FCSTD DOCUMENT  (FreeCAD 0.19R23578 (Git))
Label: carriage_assembly
License: All rights reserved
LicenseURL: http://en.wikipedia.org/wiki/All_rights_reserved
objects: App::Link×16, App::DocumentObjectGroup×2, PartDesign::CoordinateSystem×2, App::FeaturePython×1, App::Part×1
note: 2 computed .brp shape members not serialized (recipe doc carries the construction recipe); baked Part::Feature solids carry a one-line shape summary decoded from their .brp
EXTERNAL_REF file=y_axis_carriage_block.FCStd obj=Part026
EXTERNAL_REF file=x_axis_rail.FCStd obj=LCS_2
EXTERNAL_REF file=y_axis_carriage_block.FCStd obj=LCS_4
EXTERNAL_REF file=x_axis_rail.FCStd obj=Part028
EXTERNAL_REF file=x_axis_rail.FCStd obj=LCS_1
EXTERNAL_REF file=x_idler_bracket.FCStd obj=LCS_1
EXTERNAL_REF file=x_idler_bracket.FCStd obj=Part033
EXTERNAL_REF file=gates_2gt_idler_toothed.FCStd obj=LCS_1
EXTERNAL_REF file=x_idler_bracket.FCStd obj=LCS_2
EXTERNAL_REF file=gates_2gt_idler_toothed.FCStd obj=Part042
EXTERNAL_REF file=stock_motor_mount.FCStd obj=LCS_6
EXTERNAL_REF file=y_axis_carriage_block.FCStd obj=LCS_15
EXTERNAL_REF file=stock_motor_mount.FCStd obj=Part
EXTERNAL_REF file=Nema 17  Stepper Motor length 60mm.FcStd obj=LCS_0
EXTERNAL_REF file=stock_motor_mount.FCStd obj=LCS_1
EXTERNAL_REF file=Nema 17  Stepper Motor length 60mm.FcStd obj=Part
EXTERNAL_REF file=Nema 17  Stepper Motor length 60mm.FcStd obj=LCS_1
EXTERNAL_REF file=2gt_pulley_20t.FCStd obj=LCS_1
EXTERNAL_REF file=2gt_pulley_20t.FCStd obj=Part
EXTERNAL_REF file=watercooled_print_head.FCStd obj=LCS_1
EXTERNAL_REF file=x_axis_rail.FCStd obj=LCS_3
EXTERNAL_REF file=watercooled_print_head.FCStd obj=Model
EXTERNAL_REF file=Aluminum Spacer 6mm002.FCStd obj=LCS_1
EXTERNAL_REF file=y_axis_carriage_block.FCStd obj=LCS_12
EXTERNAL_REF file=Aluminum Spacer 6mm002.FCStd obj=Aluminum_Spacer_6mm002
EXTERNAL_REF file=y_axis_carriage_block.FCStd obj=LCS_11
EXTERNAL_REF file=eccentric_spacer.FCStd obj=LCS_1
EXTERNAL_REF file=y_axis_carriage_block.FCStd obj=LCS_13
EXTERNAL_REF file=eccentric_spacer.FCStd obj=Part
EXTERNAL_REF file=y_axis_carriage_block.FCStd obj=LCS_14
EXTERNAL_REF file=Aluminum Spacer 6mm002.FCStd obj=LCS_2
EXTERNAL_REF file=solid_v_wheel_assembly.FCStd obj=LCS_Origin
EXTERNAL_REF file=solid_v_wheel_assembly.FCStd obj=Model
EXTERNAL_REF file=eccentric_spacer.FCStd obj=LCS_2

FEATURE [App::DocumentObjectGroup] Parts
FEATURE [PartDesign::CoordinateSystem] LCS_Origin
  AttacherType = Attacher::AttachEngine3D
  MapMode = 2
  Support = -> [X_Axis]
FEATURE [App::DocumentObjectGroup] Constraints
FEATURE [App::FeaturePython] Variables  # WARN: FeaturePython — macro-defined, semantics opaque (R4)
FEATURE [App::Link] y_axis_carriage_block_y_axis_carriage_block001
  LinkedObject = -> <external y_axis_carriage_block.FCStd>#Part026
FEATURE [App::Link] x_axis_rail_2020_vslot_rail
  AssemblyType = Asm4EE
  AttachedBy = #LCS_2
  AttachedTo = y_axis_carriage_block_y_axis_carriage_block001#LCS_4
  AttachmentOffset = pos=(0,0,0) rot=(0,1,0;4.71239rad)
  LinkPlacement = pos=(57.675,-10,-1.34e-14) rot=(0.57735,-0.57735,0.57735;4.18879rad)
  LinkedObject = -> <external x_axis_rail.FCStd>#Part028
  Placement = pos=(57.675,-10,-1.34e-14) rot=(0.57735,-0.57735,0.57735;4.18879rad)
  expr: Placement = y_axis_carriage_block_y_axis_carriage_block001.Placement * y_axis_carriage_block#LCS_4.Placement * AttachmentOffset * x_axis_rail#LCS_2.Placement ^ -1
FEATURE [App::Link] x_idler_bracket_x_idler_bracket
  AssemblyType = Asm4EE
  AttachedBy = #LCS_1
  AttachedTo = x_axis_rail_2020_vslot_rail#LCS_1
  AttachmentOffset = pos=(0,0,0) rot=(0,0,1;4.71239rad)
  LinkPlacement = pos=(437.675,-10,-2.064e-13) rot=(0,0,1;0rad)
  LinkedObject = -> <external x_idler_bracket.FCStd>#Part033
  Placement = pos=(437.675,-10,-2.064e-13) rot=(0,0,1;0rad)
  expr: Placement = x_axis_rail_2020_vslot_rail.Placement * x_axis_rail#LCS_1.Placement * AttachmentOffset * x_idler_bracket#LCS_1.Placement ^ -1
FEATURE [App::Link] gates_2gt_idler_toothed_e3d_2gt_idler
  AssemblyType = Asm4EE
  AttachedBy = #LCS_1
  AttachedTo = x_idler_bracket_x_idler_bracket#LCS_2
  LinkPlacement = pos=(448.675,-24,-2.846e-13) rot=(-0.57735,-0.57735,-0.57735;2.0944rad)
  LinkedObject = -> <external gates_2gt_idler_toothed.FCStd>#Part042
  Placement = pos=(448.675,-24,-2.846e-13) rot=(-0.57735,-0.57735,-0.57735;2.0944rad)
  expr: Placement = x_idler_bracket_x_idler_bracket.Placement * x_idler_bracket#LCS_2.Placement * AttachmentOffset * gates_2gt_idler_toothed#LCS_1.Placement ^ -1
FEATURE [App::Link] stock_motor_mount_stock_motor_mount
  AssemblyType = Asm4EE
  AttachedBy = #LCS_6
  AttachedTo = y_axis_carriage_block_y_axis_carriage_block001#LCS_15
  LinkPlacement = pos=(9.35,-23,-36) rot=(0.57735,0.57735,0.57735;4.18879rad)
  LinkedObject = -> <external stock_motor_mount.FCStd>#Part
  Placement = pos=(9.35,-23,-36) rot=(0.57735,0.57735,0.57735;4.18879rad)
  expr: Placement = y_axis_carriage_block_y_axis_carriage_block001.Placement * y_axis_carriage_block#LCS_15.Placement * AttachmentOffset * stock_motor_mount#LCS_6.Placement ^ -1
FEATURE [App::Link] Nema_17__Stepper_Motor_length_60mm_Nema_17__Stepper_Motor_length_60mm  label="Nema_17__Stepper_Motor_length_60mm_Nema 17  Stepper Motor length 60mm"
  AssemblyType = Asm4EE
  AttachedBy = #LCS_0
  AttachedTo = stock_motor_mount_stock_motor_mount#LCS_1
  AttachmentOffset = pos=(0,0,0) rot=(1,0,0;3.14159rad)
  LinkPlacement = pos=(36.33,-23,73.42) rot=(0,0.707107,0.707107;3.14159rad)
  LinkedObject = -> <external Nema 17  Stepper Motor length 60mm.FcStd>#Part
  Placement = pos=(36.33,-23,73.42) rot=(0,0.707107,0.707107;3.14159rad)
  expr: Placement = stock_motor_mount_stock_motor_mount.Placement * stock_motor_mount#LCS_1.Placement * AttachmentOffset * Nema_17__Stepper_Motor_length_60mm#LCS_0.Placement ^ -1
FEATURE [App::Link] _gt_pulley_20t_2gt_pulley_20t
  AssemblyType = Asm4EE
  AttachedBy = #LCS_1
  AttachedTo = Nema_17__Stepper_Motor_length_60mm_Nema_17__Stepper_Motor_length_60mm#LCS_1
  AttachmentOffset = pos=(0,0,0) rot=(1,0,0;3.14159rad)
  LinkPlacement = pos=(36.33,-23,-10.18) rot=(-0.57735,-0.57735,-0.57735;2.0944rad)
  LinkedObject = -> <external 2gt_pulley_20t.FCStd>#Part
  Placement = pos=(36.33,-23,-10.18) rot=(-0.57735,-0.57735,-0.57735;2.0944rad)
  expr: Placement = Nema_17__Stepper_Motor_length_60mm_Nema_17__Stepper_Motor_length_60mm.Placement * Nema_17__Stepper_Motor_length_60mm#LCS_1.Placement * AttachmentOffset * _gt_pulley_20t#LCS_1.Placement ^ -1
FEATURE [App::Link] watercooled_print_head
  AssemblyType = Asm4EE
  AttachedBy = #LCS_1
  AttachedTo = x_axis_rail_2020_vslot_rail#LCS_3
  AttachmentOffset = pos=(0,0,0) rot=(0.57735,-0.57735,0.57735;2.0944rad)
  LinkPlacement = pos=(241.675,-40,-25) rot=(0,0,1;0rad)
  LinkedObject = -> <external watercooled_print_head.FCStd>#Model
  Placement = pos=(241.675,-40,-25) rot=(0,0,1;0rad)
  expr: Placement = x_axis_rail_2020_vslot_rail.Placement * x_axis_rail#LCS_3.Placement * AttachmentOffset * watercooled_print_head#LCS_1.Placement ^ -1
FEATURE [App::Link] Aluminum_Spacer_6mm002_Aluminum_Spacer_6mm002
  AssemblyType = Asm4EE
  AttachedBy = #LCS_1
  AttachedTo = y_axis_carriage_block_y_axis_carriage_block001#LCS_12
  LinkPlacement = pos=(-6,40,49.85) rot=(0,-1,0;4.71239rad)
  LinkedObject = -> <external Aluminum Spacer 6mm002.FCStd>#Aluminum_Spacer_6mm002
  Placement = pos=(-6,40,49.85) rot=(0,-1,0;4.71239rad)
  expr: Placement = y_axis_carriage_block_y_axis_carriage_block001.Placement * y_axis_carriage_block#LCS_12.Placement * AttachmentOffset * Aluminum_Spacer_6mm002#LCS_1.Placement ^ -1
FEATURE [App::Link] Aluminum_Spacer_6mm002_Aluminum_Spacer_6mm003
  AssemblyType = Asm4EE
  AttachedBy = #LCS_1
  AttachedTo = y_axis_carriage_block_y_axis_carriage_block001#LCS_11
  LinkPlacement = pos=(-6,-40,49.85) rot=(0,-1,0;4.71239rad)
  LinkedObject = -> <external Aluminum Spacer 6mm002.FCStd>#Aluminum_Spacer_6mm002
  Placement = pos=(-6,-40,49.85) rot=(0,-1,0;4.71239rad)
  expr: Placement = y_axis_carriage_block_y_axis_carriage_block001.Placement * y_axis_carriage_block#LCS_11.Placement * AttachmentOffset * Aluminum_Spacer_6mm002#LCS_1.Placement ^ -1
FEATURE [App::Link] eccentric_spacer_eccentric_spacer
  AssemblyType = Asm4EE
  AttachedBy = #LCS_1
  AttachedTo = y_axis_carriage_block_y_axis_carriage_block001#LCS_13
  AttachmentOffset = pos=(0,0,0) rot=(1,0,0;3.14159rad)
  LinkPlacement = pos=(0,40,-49.85) rot=(-0.707107,0,0.707107;3.14159rad)
  LinkedObject = -> <external eccentric_spacer.FCStd>#Part
  Placement = pos=(0,40,-49.85) rot=(-0.707107,0,0.707107;3.14159rad)
  expr: Placement = y_axis_carriage_block_y_axis_carriage_block001.Placement * y_axis_carriage_block#LCS_13.Placement * AttachmentOffset * eccentric_spacer#LCS_1.Placement ^ -1
FEATURE [App::Link] eccentric_spacer_eccentric_spacer_2
  AssemblyType = Asm4EE
  AttachedBy = #LCS_1
  AttachedTo = y_axis_carriage_block_y_axis_carriage_block001#LCS_14
  AttachmentOffset = pos=(0,0,0) rot=(0,-1,0;3.14159rad)
  LinkPlacement = pos=(0,-40,-49.85) rot=(0,-1,0;1.5708rad)
  LinkedObject = -> <external eccentric_spacer.FCStd>#Part
  Placement = pos=(0,-40,-49.85) rot=(0,-1,0;1.5708rad)
  expr: Placement = y_axis_carriage_block_y_axis_carriage_block001.Placement * y_axis_carriage_block#LCS_14.Placement * AttachmentOffset * eccentric_spacer#LCS_1.Placement ^ -1
FEATURE [App::Link] solid_v_wheel_assembly
  AssemblyType = Asm4EE
  AttachedBy = #LCS_Origin
  AttachedTo = Aluminum_Spacer_6mm002_Aluminum_Spacer_6mm002#LCS_2
  LinkPlacement = pos=(-6,40,49.85) rot=(0.57735,-0.57735,0.57735;4.18879rad)
  LinkedObject = -> <external solid_v_wheel_assembly.FCStd>#Model
  Placement = pos=(-6,40,49.85) rot=(0.57735,-0.57735,0.57735;4.18879rad)
  expr: Placement = Aluminum_Spacer_6mm002_Aluminum_Spacer_6mm002.Placement * Aluminum_Spacer_6mm002#LCS_2.Placement * AttachmentOffset * solid_v_wheel_assembly#LCS_Origin.Placement ^ -1
FEATURE [App::Link] solid_v_wheel_assembly_2
  AssemblyType = Asm4EE
  AttachedBy = #LCS_Origin
  AttachedTo = Aluminum_Spacer_6mm002_Aluminum_Spacer_6mm003#LCS_2
  LinkPlacement = pos=(-6,-40,49.85) rot=(0.57735,-0.57735,0.57735;4.18879rad)
  LinkedObject = -> <external solid_v_wheel_assembly.FCStd>#Model
  Placement = pos=(-6,-40,49.85) rot=(0.57735,-0.57735,0.57735;4.18879rad)
  expr: Placement = Aluminum_Spacer_6mm002_Aluminum_Spacer_6mm003.Placement * Aluminum_Spacer_6mm002#LCS_2.Placement * AttachmentOffset * solid_v_wheel_assembly#LCS_Origin.Placement ^ -1
FEATURE [App::Link] solid_v_wheel_assembly_3
  AssemblyType = Asm4EE
  AttachedBy = #LCS_Origin
  AttachedTo = eccentric_spacer_eccentric_spacer#LCS_2
  AttachmentOffset = pos=(0,0,0) rot=(0,-1,0;3.14159rad)
  LinkPlacement = pos=(-6,40.78,-49.85) rot=(0.57735,0.57735,0.57735;2.0944rad)
  LinkedObject = -> <external solid_v_wheel_assembly.FCStd>#Model
  Placement = pos=(-6,40.78,-49.85) rot=(0.57735,0.57735,0.57735;2.0944rad)
  expr: Placement = eccentric_spacer_eccentric_spacer.Placement * eccentric_spacer#LCS_2.Placement * AttachmentOffset * solid_v_wheel_assembly#LCS_Origin.Placement ^ -1
FEATURE [App::Link] solid_v_wheel_assembly_4
  AssemblyType = Asm4EE
  AttachedBy = #LCS_Origin
  AttachedTo = eccentric_spacer_eccentric_spacer_2#LCS_2
  AttachmentOffset = pos=(0,0,0) rot=(0,1,0;3.14159rad)
  LinkPlacement = pos=(-6,-40.78,-49.85) rot=(-0.57735,0.57735,-0.57735;2.0944rad)
  LinkedObject = -> <external solid_v_wheel_assembly.FCStd>#Model
  Placement = pos=(-6,-40.78,-49.85) rot=(-0.57735,0.57735,-0.57735;2.0944rad)
  expr: Placement = eccentric_spacer_eccentric_spacer_2.Placement * eccentric_spacer#LCS_2.Placement * AttachmentOffset * solid_v_wheel_assembly#LCS_Origin.Placement ^ -1
FEATURE [PartDesign::CoordinateSystem] LCS_1
  AttacherType = Attacher::AttachEngine3D
  AttachmentOffset = pos=(-11.5,0,0) rot=(0,0,1;0rad)
  MapMode = 2
  Placement = pos=(-11.5,0,0) rot=(0,0,1;0rad)
  Support = -> [LCS_Origin]
FEATURE [App::Part] Model
  Configuration = 0
  Group = -> [LCS_Origin,Constraints,Variables,y_axis_carriage_block_y_axis_carriage_block001,x_axis_rail_2020_vslot_rail,x_idler_bracket_x_idler_bracket,gates_2gt_idler_toothed_e3d_2gt_idler,stock_motor_mount_stock_motor_mount,Nema_17__Stepper_Motor_length_60mm_Nema_17__Stepper_Motor_length_60mm,_gt_pulley_20t_2gt_pulley_20t,watercooled_print_head,Aluminum_Spacer_6mm002_Aluminum_Spacer_6mm002,+8 more]
  Origin = -> Origin
  Type = Assembly4 Model

RESOLVED EXTERNAL PARTS (link-assembly join: the EXTERNAL_REF files above that resolve inside this repo's crawl, each included once):
---- part gates_2gt_idler_toothed.FCStd = doc fcstd_5f911b90b553 ----
FCSTD DOCUMENT  (FreeCAD 0.19R23578 (Git))
Label: gates_2gt_idler_toothed
License: All rights reserved
LicenseURL: http://en.wikipedia.org/wiki/All_rights_reserved
objects: Sketcher::SketchObject×1, PartDesign::Revolution×1, PartDesign::Body×1, PartDesign::CoordinateSystem×1, App::Part×1
note: 5 computed .brp shape members not serialized (recipe doc carries the construction recipe); baked Part::Feature solids carry a one-line shape summary decoded from their .brp

FEATURE [Sketcher::SketchObject] Sketch069
  MapMode = 5
  Support = -> [XY_Plane079]
  sketch-geometry (8):
    g0: LineSegment StartX=-3.5 StartY=7.5 StartZ=0 EndX=-3.5 EndY=6.11 EndZ=0
    g1: LineSegment StartX=-3.5 StartY=6.11 StartZ=0 EndX=3.5 EndY=6.11 EndZ=0
    g2: LineSegment StartX=3.5 StartY=6.11 StartZ=0 EndX=3.5 EndY=7.5 EndZ=0
    g3: LineSegment StartX=3.5 StartY=7.5 StartZ=0 EndX=5 EndY=7.5 EndZ=0
    g4: LineSegment StartX=5 StartY=7.5 StartZ=0 EndX=5 EndY=2.5 EndZ=0
    g5: LineSegment StartX=5 StartY=2.5 StartZ=0 EndX=-5 EndY=2.5 EndZ=0
    g6: LineSegment StartX=-5 StartY=2.5 StartZ=0 EndX=-5 EndY=7.5 EndZ=0
    g7: LineSegment StartX=-5 StartY=7.5 StartZ=0 EndX=-3.5 EndY=7.5 EndZ=0
  constraints (20):
    c: Coincident(g0,g1)
    c: Coincident(g1,g2)
    c: Coincident(g2,g3)
    c: Horizontal(g3)
    c: Coincident(g3,g4)
    c: Coincident(g4,g5)
    c: Coincident(g5,g6)
    c: Coincident(g6,g7)
    c: Coincident(g0,g7)
    c: Vertical(g6)
    c: Vertical(g0)
    c: Symmetric(g0,g1,g-2)
    c: Symmetric(g0,g2,g-2)
    c: Symmetric(g6,g3,g-2)
    c: Symmetric(g5,g4,g-2)
    c: DistanceX(g1,g1) = 7
    c: DistanceX(g5,g5) = 10
    c: DistanceY(g-1,g4) = 2.5
    c: DistanceY(g-1,g1) = 6.11
    c: DistanceY(g-1,g3) = 7.5
FEATURE [PartDesign::Revolution] Revolution002
  AllowMultiFace = false
  Angle = 360
  Axis = (1,0,0)
  Base = (0,0,0)
  Profile = -> Sketch069
  ReferenceAxis = -> X_Axis079
FEATURE [PartDesign::Body] Body025  label="Body"
  Group = -> [Sketch069,Revolution002]
  Origin = -> Origin079
  Tip = -> Revolution002
FEATURE [PartDesign::CoordinateSystem] LCS_1
  AttacherType = Attacher::AttachEngine3D
  MapMode = 45
  Placement = pos=(0,1.19e-14,1e-16) rot=(-0.57735,-0.57735,-0.57735;2.0944rad)
  Support = -> [Revolution002]
FEATURE [App::Part] Part042  label="e3d_2gt_idler"
  Group = -> [Body025,LCS_1]
  Origin = -> Origin078
---- part solid_v_wheel_assembly.FCStd = doc fcstd_e9b3de996b96 ----
FCSTD DOCUMENT  (FreeCAD 0.19R21858 (Git))
Label: solid_v_wheel_assembly
License: All rights reserved
LicenseURL: http://en.wikipedia.org/wiki/All_rights_reserved
objects: App::Link×3, App::DocumentObjectGroup×2, PartDesign::CoordinateSystem×1, App::FeaturePython×1, App::Part×1
note: 1 computed .brp shape members not serialized (recipe doc carries the construction recipe); baked Part::Feature solids carry a one-line shape summary decoded from their .brp
EXTERNAL_REF file=625RS_bearing.FCStd obj=LCS_2
EXTERNAL_REF file=delrin_solid_v-wheel.FCStd obj=LCS_1
EXTERNAL_REF file=delrin_solid_v-wheel.FCStd obj=Part
EXTERNAL_REF file=625RS_bearing.FCStd obj=LCS_1
EXTERNAL_REF file=625RS_bearing.FCStd obj=Part
EXTERNAL_REF file=delrin_solid_v-wheel.FCStd obj=LCS_2

FEATURE [App::DocumentObjectGroup] Parts
FEATURE [PartDesign::CoordinateSystem] LCS_Origin
  AttacherType = Attacher::AttachEngine3D
  MapMode = 2
  Support = -> [X_Axis]
FEATURE [App::DocumentObjectGroup] Constraints
FEATURE [App::FeaturePython] Variables  # WARN: FeaturePython — macro-defined, semantics opaque (R4)
FEATURE [App::Link] delrin_solid_v_wheel_delrin_solid_v_wheel  label="delrin_solid_v_wheel_delrin_solid_v-wheel"
  AssemblyType = Asm4EE
  AttachedBy = #LCS_1
  AttachedTo = _25RS_bearing_625RS_bearing#LCS_2
  LinkPlacement = pos=(-4e-16,3e-16,-5.5) rot=(0.57735,-0.57735,0.57735;2.0944rad)
  LinkedObject = -> <external delrin_solid_v-wheel.FCStd>#Part
  Placement = pos=(-4e-16,3e-16,-5.5) rot=(0.57735,-0.57735,0.57735;2.0944rad)
  expr: Placement = _25RS_bearing_625RS_bearing.Placement * _25RS_bearing#LCS_2.Placement * AttachmentOffset * delrin_solid_v_wheel#LCS_1.Placement ^ -1
FEATURE [App::Link] _25RS_bearing_625RS_bearing
  AssemblyType = Asm4EE
  AttachedBy = #LCS_1
  AttachedTo = Parent Assembly#LCS_Origin
  LinkPlacement = pos=(-1e-16,1e-16,-2.5) rot=(-0.57735,-0.57735,-0.57735;2.0944rad)
  LinkedObject = -> <external 625RS_bearing.FCStd>#Part
  Placement = pos=(-1e-16,1e-16,-2.5) rot=(-0.57735,-0.57735,-0.57735;2.0944rad)
  expr: Placement = LCS_Origin.Placement * AttachmentOffset * _25RS_bearing#LCS_1.Placement ^ -1
FEATURE [App::Link] _25RS_bearing_625RS_bearing_2
  AssemblyType = Asm4EE
  AttachedBy = #LCS_2
  AttachedTo = delrin_solid_v_wheel_delrin_solid_v_wheel#LCS_2
  AttachmentOffset = pos=(0,0,0) rot=(1,0,0;3.14159rad)
  LinkPlacement = pos=(2e-16,1.4e-15,-8.5) rot=(0.57735,0.57735,-0.57735;2.0944rad)
  LinkedObject = -> <external 625RS_bearing.FCStd>#Part
  Placement = pos=(2e-16,1.4e-15,-8.5) rot=(0.57735,0.57735,-0.57735;2.0944rad)
  expr: Placement = delrin_solid_v_wheel_delrin_solid_v_wheel.Placement * delrin_solid_v_wheel#LCS_2.Placement * AttachmentOffset * _25RS_bearing#LCS_2.Placement ^ -1
FEATURE [App::Part] Model
  Configuration = 0
  Group = -> [LCS_Origin,Constraints,Variables,delrin_solid_v_wheel_delrin_solid_v_wheel,_25RS_bearing_625RS_bearing,_25RS_bearing_625RS_bearing_2]
  Origin = -> Origin
  Type = Assembly4 Model
---- part watercooled_print_head.FCStd = doc fcstd_21ffa87f471e ----
FCSTD DOCUMENT  (FreeCAD 0.19R24267 (Git))
Label: watercooled_print_head
License: All rights reserved
LicenseURL: http://en.wikipedia.org/wiki/All_rights_reserved
objects: App::Link×26, Part::FeaturePython×3, App::DocumentObjectGroup×2, PartDesign::CoordinateSystem×2, App::FeaturePython×1, App::Part×1
note: 5 computed .brp shape members not serialized (recipe doc carries the construction recipe); baked Part::Feature solids carry a one-line shape summary decoded from their .brp
EXTERNAL_REF file=watercooled_block.FCStd obj=LCS_7
EXTERNAL_REF file=watercooled_block.FCStd obj=Part
EXTERNAL_REF file=barb_fitting LC-0640-M6.FCStd obj=LCS_1
EXTERNAL_REF file=watercooled_block.FCStd obj=LCS_4
EXTERNAL_REF file=barb_fitting LC-0640-M6.FCStd obj=Part
EXTERNAL_REF file=watercooled_block.FCStd obj=LCS_5
EXTERNAL_REF file=eccentric_spacer.FCStd obj=LCS_1
EXTERNAL_REF file=watercooled_block.FCStd obj=LCS_9
EXTERNAL_REF file=eccentric_spacer.FCStd obj=Part
EXTERNAL_REF file=watercooled_block.FCStd obj=LCS_10
EXTERNAL_REF file=plug_fitting_MSWZ6.FCStd obj=LCS_1
EXTERNAL_REF file=watercooled_block.FCStd obj=LCS_3
EXTERNAL_REF file=plug_fitting_MSWZ6.FCStd obj=Part
EXTERNAL_REF file=e3d_volcano_assembly.FCStd obj=LCS_Origin
EXTERNAL_REF file=e3d_volcano_assembly.FCStd obj=Model
EXTERNAL_REF file=G5_extruder.FCStd obj=LCS_5
EXTERNAL_REF file=watercooled_block.FCStd obj=LCS_6
EXTERNAL_REF file=G5_extruder.FCStd obj=Model
EXTERNAL_REF file=eccentric_spacer.FCStd obj=LCS_2
EXTERNAL_REF file=precision_spacer.FCStd obj=LCS_2
EXTERNAL_REF file=precision_spacer.FCStd obj=Part
EXTERNAL_REF file=105zz_ball_bearing.FCStd obj=LCS_2
EXTERNAL_REF file=precision_spacer.FCStd obj=LCS_1
EXTERNAL_REF file=105zz_ball_bearing.FCStd obj=_05zz_ball_bearing
EXTERNAL_REF file=105zz_ball_bearing.FCStd obj=LCS_1
EXTERNAL_REF file=micro_v_wheel.FCStd obj=LCS_2
EXTERNAL_REF file=micro_v_wheel.FCStd obj=delrin_wheel
EXTERNAL_REF file=micro_v_wheel.FCStd obj=LCS_1
EXTERNAL_REF file=Aluminum Spacer 6mm002.FCStd obj=LCS_1
EXTERNAL_REF file=watercooled_block.FCStd obj=LCS_8
EXTERNAL_REF file=Aluminum Spacer 6mm002.FCStd obj=Aluminum_Spacer_6mm002
EXTERNAL_REF file=Aluminum Spacer 6mm002.FCStd obj=LCS_2
EXTERNAL_REF file=barb_fitting LC-0640-M6.FCStd obj=LCS_2
EXTERNAL_REF file=silicone_tube.FCStd obj=LCS_1
EXTERNAL_REF file=silicone_tube.FCStd obj=Part
EXTERNAL_REF file=openbuilds_low_profile_screws.FCStd obj=LCS_0
EXTERNAL_REF file=watercooled_block.FCStd obj=LCS_1
EXTERNAL_REF file=openbuilds_low_profile_screws.FCStd obj=low_profile_screw_l25mm
EXTERNAL_REF file=watercooled_block.FCStd obj=LCS_2
EXTERNAL_REF file=part_cooling_duct.FCStd obj=Part

FEATURE [App::DocumentObjectGroup] Parts
FEATURE [PartDesign::CoordinateSystem] LCS_Origin
  AttacherType = Attacher::AttachEngine3D
  MapMode = 2
  Support = -> [X_Axis]
FEATURE [App::DocumentObjectGroup] Constraints
FEATURE [App::FeaturePython] Variables  # WARN: FeaturePython — macro-defined, semantics opaque (R4)
FEATURE [App::Link] watercooled_block_watercooled_block
  AssemblyType = Asm4EE
  AttachedBy = #LCS_7
  AttachedTo = Parent Assembly#LCS_Origin
  AttachmentOffset = pos=(0,0,0) rot=(1,0,0;3.14159rad)
  LinkPlacement = pos=(6,3.3e-15,2.6e-15) rot=(0,0,-1;1.5708rad)
  LinkedObject = -> <external watercooled_block.FCStd>#Part
  Placement = pos=(6,3.3e-15,2.6e-15) rot=(0,0,-1;1.5708rad)
  expr: Placement = LCS_Origin.Placement * AttachmentOffset * watercooled_block#LCS_7.Placement ^ -1
FEATURE [App::Link] barb_fitting_LC_0640_M6_barb_fitting_LC_0640_M6  label="barb_fitting_LC_0640_M6_barb_fitting LC-0640-M6"
  AssemblyType = Asm4EE
  AttachedBy = #LCS_1
  AttachedTo = watercooled_block_watercooled_block#LCS_4
  LinkPlacement = pos=(14,-6.35,5.5) rot=(0.57735,0.57735,0.57735;2.0944rad)
  LinkedObject = -> <external barb_fitting LC-0640-M6.FCStd>#Part
  Placement = pos=(14,-6.35,5.5) rot=(0.57735,0.57735,0.57735;2.0944rad)
  expr: Placement = watercooled_block_watercooled_block.Placement * watercooled_block#LCS_4.Placement * AttachmentOffset * barb_fitting_LC_0640_M6#LCS_1.Placement ^ -1
FEATURE [App::Link] barb_fitting_LC_0640_M6_barb_fitting_LC_0640_M6001  label="barb_fitting_LC_0640_M6_barb_fitting LC-0640-M007"
  AssemblyType = Asm4EE
  AttachedBy = #LCS_1
  AttachedTo = watercooled_block_watercooled_block#LCS_5
  LinkPlacement = pos=(14,6.35,5.5) rot=(0.57735,0.57735,0.57735;2.0944rad)
  LinkedObject = -> <external barb_fitting LC-0640-M6.FCStd>#Part
  Placement = pos=(14,6.35,5.5) rot=(0.57735,0.57735,0.57735;2.0944rad)
  expr: Placement = watercooled_block_watercooled_block.Placement * watercooled_block#LCS_5.Placement * AttachmentOffset * barb_fitting_LC_0640_M6#LCS_1.Placement ^ -1
FEATURE [App::Link] eccentric_spacer_eccentric_spacer
  AssemblyType = Asm4EE
  AttachedBy = #LCS_1
  AttachedTo = watercooled_block_watercooled_block#LCS_9
  AttachmentOffset = pos=(0,0,0) rot=(0.707107,-0.707107,0;3.14159rad)
  LinkPlacement = pos=(-9,18.35,40.95) rot=(0.57735,0.57735,0.57735;4.18879rad)
  LinkedObject = -> <external eccentric_spacer.FCStd>#Part
  Placement = pos=(-9,18.35,40.95) rot=(0.57735,0.57735,0.57735;4.18879rad)
  expr: Placement = watercooled_block_watercooled_block.Placement * watercooled_block#LCS_9.Placement * AttachmentOffset * eccentric_spacer#LCS_1.Placement ^ -1
FEATURE [App::Link] eccentric_spacer_eccentric_spacer_2
  AssemblyType = Asm4EE
  AttachedBy = #LCS_1
  AttachedTo = watercooled_block_watercooled_block#LCS_10
  AttachmentOffset = pos=(0,0,0) rot=(0.707107,0.707107,0;3.14159rad)
  LinkPlacement = pos=(21,18.35,40.95) rot=(0.57735,-0.57735,-0.57735;4.18879rad)
  LinkedObject = -> <external eccentric_spacer.FCStd>#Part
  Placement = pos=(21,18.35,40.95) rot=(0.57735,-0.57735,-0.57735;4.18879rad)
  expr: Placement = watercooled_block_watercooled_block.Placement * watercooled_block#LCS_10.Placement * AttachmentOffset * eccentric_spacer#LCS_1.Placement ^ -1
FEATURE [App::Link] plug_fitting_MSWZ6_plug_fitting_MSWZ6
  AssemblyType = Asm4EE
  AttachedBy = #LCS_1
  AttachedTo = watercooled_block_watercooled_block#LCS_3
  AttachmentOffset = pos=(0,0,0) rot=(1,0,0;3.14159rad)
  LinkPlacement = pos=(-10,14.35,5.5) rot=(0.57735,-0.57735,-0.57735;2.0944rad)
  LinkedObject = -> <external plug_fitting_MSWZ6.FCStd>#Part
  Placement = pos=(-10,14.35,5.5) rot=(0.57735,-0.57735,-0.57735;2.0944rad)
  expr: Placement = watercooled_block_watercooled_block.Placement * watercooled_block#LCS_3.Placement * AttachmentOffset * plug_fitting_MSWZ6#LCS_1.Placement ^ -1
FEATURE [App::Link] e3d_volcano_assembly
  AssemblyType = Asm4EE
  AttachedBy = #LCS_Origin
  AttachedTo = watercooled_block_watercooled_block#LCS_7
  AttachmentOffset = pos=(0,0,0) rot=(1,0,0;3.14159rad)
  LinkPlacement = pos=(0,6e-16,0) rot=(0,0,1;0rad)
  LinkedObject = -> <external e3d_volcano_assembly.FCStd>#Model
  Placement = pos=(0,6e-16,0) rot=(0,0,1;0rad)
  expr: Placement = watercooled_block_watercooled_block.Placement * watercooled_block#LCS_7.Placement * AttachmentOffset * e3d_volcano_assembly#LCS_Origin.Placement ^ -1
FEATURE [App::Link] G5_extruder
  AssemblyType = Asm4EE
  AttachedBy = #LCS_5
  AttachedTo = watercooled_block_watercooled_block#LCS_6
  AttachmentOffset = pos=(0,0,0) rot=(0.707107,-0.707107,0;3.14159rad)
  LinkPlacement = pos=(-0.02386,0.00620281,15) rot=(0,0,-1;1.5708rad)
  LinkedObject = -> <external G5_extruder.FCStd>#Model
  Placement = pos=(-0.02386,0.00620281,15) rot=(0,0,-1;1.5708rad)
  expr: Placement = watercooled_block_watercooled_block.Placement * watercooled_block#LCS_6.Placement * AttachmentOffset * G5_extruder#LCS_5.Placement ^ -1
FEATURE [App::Link] precision_spacer_precision_spacer
  AssemblyType = Asm4EE
  AttachedBy = #LCS_2
  AttachedTo = eccentric_spacer_eccentric_spacer#LCS_2
  LinkPlacement = pos=(-9.78,24.35,40.95) rot=(0.57735,0.57735,0.57735;4.18879rad)
  LinkedObject = -> <external precision_spacer.FCStd>#Part
  Placement = pos=(-9.78,24.35,40.95) rot=(0.57735,0.57735,0.57735;4.18879rad)
  expr: Placement = eccentric_spacer_eccentric_spacer.Placement * eccentric_spacer#LCS_2.Placement * AttachmentOffset * precision_spacer#LCS_2.Placement ^ -1
FEATURE [App::Link] precision_spacer_precision_spacer_2
  AssemblyType = Asm4EE
  AttachedBy = #LCS_2
  AttachedTo = eccentric_spacer_eccentric_spacer_2#LCS_2
  LinkPlacement = pos=(21.78,24.35,40.95) rot=(0.57735,-0.57735,-0.57735;4.18879rad)
  LinkedObject = -> <external precision_spacer.FCStd>#Part
  Placement = pos=(21.78,24.35,40.95) rot=(0.57735,-0.57735,-0.57735;4.18879rad)
  expr: Placement = eccentric_spacer_eccentric_spacer_2.Placement * eccentric_spacer#LCS_2.Placement * AttachmentOffset * precision_spacer#LCS_2.Placement ^ -1
FEATURE [App::Link] _05zz_ball_bearing_105zz_ball_bearing
  AssemblyType = Asm4EE
  AttachedBy = #LCS_2
  AttachedTo = precision_spacer_precision_spacer#LCS_1
  LinkPlacement = pos=(-9.78,25.35,40.95) rot=(0,0,-1;4.71239rad)
  LinkedObject = -> <external 105zz_ball_bearing.FCStd>#_05zz_ball_bearing
  Placement = pos=(-9.78,25.35,40.95) rot=(0,0,-1;4.71239rad)
  expr: Placement = precision_spacer_precision_spacer.Placement * precision_spacer#LCS_1.Placement * AttachmentOffset * _05zz_ball_bearing#LCS_2.Placement ^ -1
FEATURE [App::Link] _05zz_ball_bearing_105zz_ball_bearing_2
  AssemblyType = Asm4EE
  AttachedBy = #LCS_2
  AttachedTo = precision_spacer_precision_spacer_2#LCS_1
  LinkPlacement = pos=(21.78,25.35,40.95) rot=(-0.707107,-0.707107,0;3.14159rad)
  LinkedObject = -> <external 105zz_ball_bearing.FCStd>#_05zz_ball_bearing
  Placement = pos=(21.78,25.35,40.95) rot=(-0.707107,-0.707107,0;3.14159rad)
  expr: Placement = precision_spacer_precision_spacer_2.Placement * precision_spacer#LCS_1.Placement * AttachmentOffset * _05zz_ball_bearing#LCS_2.Placement ^ -1
FEATURE [App::Link] micro_v_wheel_micro_v_wheel
  AssemblyType = Asm4EE
  AttachedBy = #LCS_2
  AttachedTo = _05zz_ball_bearing_105zz_ball_bearing#LCS_1
  LinkPlacement = pos=(-9.78,25.45,40.95) rot=(0,0,1;1.5708rad)
  LinkedObject = -> <external micro_v_wheel.FCStd>#delrin_wheel
  Placement = pos=(-9.78,25.45,40.95) rot=(0,0,1;1.5708rad)
  expr: Placement = _05zz_ball_bearing_105zz_ball_bearing.Placement * _05zz_ball_bearing#LCS_1.Placement * AttachmentOffset * micro_v_wheel#LCS_2.Placement ^ -1
FEATURE [App::Link] micro_v_wheel_micro_v_wheel_2
  AssemblyType = Asm4EE
  AttachedBy = #LCS_2
  AttachedTo = _05zz_ball_bearing_105zz_ball_bearing_2#LCS_1
  LinkPlacement = pos=(21.78,25.45,40.95) rot=(0.707107,0.707107,0;3.14159rad)
  LinkedObject = -> <external micro_v_wheel.FCStd>#delrin_wheel
  Placement = pos=(21.78,25.45,40.95) rot=(0.707107,0.707107,0;3.14159rad)
  expr: Placement = _05zz_ball_bearing_105zz_ball_bearing_2.Placement * _05zz_ball_bearing#LCS_1.Placement * AttachmentOffset * micro_v_wheel#LCS_2.Placement ^ -1
FEATURE [App::Link] _05zz_ball_bearing_105zz_ball_bearing001
  AssemblyType = Asm4EE
  AttachedBy = #LCS_2
  AttachedTo = micro_v_wheel_micro_v_wheel#LCS_1
  LinkPlacement = pos=(-9.78,30.35,40.95) rot=(0,0,-1;4.71239rad)
  LinkedObject = -> <external 105zz_ball_bearing.FCStd>#_05zz_ball_bearing
  Placement = pos=(-9.78,30.35,40.95) rot=(0,0,-1;4.71239rad)
  expr: Placement = micro_v_wheel_micro_v_wheel.Placement * micro_v_wheel#LCS_1.Placement * AttachmentOffset * _05zz_ball_bearing#LCS_2.Placement ^ -1
FEATURE [App::Link] _05zz_ball_bearing_105zz_ball_bearing002
  AssemblyType = Asm4EE
  AttachedBy = #LCS_2
  AttachedTo = micro_v_wheel_micro_v_wheel_2#LCS_1
  LinkPlacement = pos=(21.78,30.35,40.95) rot=(-0.707107,-0.707107,0;3.14159rad)
  LinkedObject = -> <external 105zz_ball_bearing.FCStd>#_05zz_ball_bearing
  Placement = pos=(21.78,30.35,40.95) rot=(-0.707107,-0.707107,0;3.14159rad)
  expr: Placement = micro_v_wheel_micro_v_wheel_2.Placement * micro_v_wheel#LCS_1.Placement * AttachmentOffset * _05zz_ball_bearing#LCS_2.Placement ^ -1
FEATURE [Part::FeaturePython] Nut  label="M5-Nut"  # Fasteners workbench fastener (typed FeaturePython)
  AssemblyType = Asm4EE
  AttachedBy = Origin
  AttachedTo = _05zz_ball_bearing_105zz_ball_bearing001#LCS_1
  Placement = pos=(-9.78,34.35,40.95) rot=(-1,0,0;1.5708rad)
  diameter = 3
  invert = false
  matchOuter = false
  offset = 0
  thread = false
  type = 5
  expr: Placement = _05zz_ball_bearing_105zz_ball_bearing001.Placement * _05zz_ball_bearing#LCS_1.Placement * AttachmentOffset
FEATURE [Part::FeaturePython] Nut001  label="M5-Nut001"  # Fasteners workbench fastener (typed FeaturePython)
  AssemblyType = Asm4EE
  AttachedBy = Origin
  AttachedTo = _05zz_ball_bearing_105zz_ball_bearing002#LCS_1
  Placement = pos=(21.78,34.35,40.95) rot=(0,0.707107,0.707107;3.14159rad)
  diameter = 3
  invert = false
  matchOuter = false
  offset = 0
  thread = false
  type = 5
  expr: Placement = _05zz_ball_bearing_105zz_ball_bearing002.Placement * _05zz_ball_bearing#LCS_1.Placement * AttachmentOffset
FEATURE [App::Link] Aluminum_Spacer_6mm002_Aluminum_Spacer_6mm002
  AssemblyType = Asm4EE
  AttachedBy = #LCS_1
  AttachedTo = watercooled_block_watercooled_block#LCS_8
  LinkPlacement = pos=(6,24.35,9.05) rot=(0,0.707107,-0.707107;3.14159rad)
  LinkedObject = -> <external Aluminum Spacer 6mm002.FCStd>#Aluminum_Spacer_6mm002
  Placement = pos=(6,24.35,9.05) rot=(0,0.707107,-0.707107;3.14159rad)
  expr: Placement = watercooled_block_watercooled_block.Placement * watercooled_block#LCS_8.Placement * AttachmentOffset * Aluminum_Spacer_6mm002#LCS_1.Placement ^ -1
FEATURE [App::Link] precision_spacer_precision_spacer001
  AssemblyType = Asm4EE
  AttachedBy = #LCS_1
  AttachedTo = Aluminum_Spacer_6mm002_Aluminum_Spacer_6mm002#LCS_2
  LinkPlacement = pos=(6,25.35,9.05) rot=(-1,0,0;4.71239rad)
  LinkedObject = -> <external precision_spacer.FCStd>#Part
  Placement = pos=(6,25.35,9.05) rot=(-1,0,0;4.71239rad)
  expr: Placement = Aluminum_Spacer_6mm002_Aluminum_Spacer_6mm002.Placement * Aluminum_Spacer_6mm002#LCS_2.Placement * AttachmentOffset * precision_spacer#LCS_1.Placement ^ -1
FEATURE [App::Link] _05zz_ball_bearing_105zz_ball_bearing003
  AssemblyType = Asm4EE
  AttachedBy = #LCS_1
  AttachedTo = precision_spacer_precision_spacer001#LCS_2
  LinkPlacement = pos=(6,29.35,9.05) rot=(-0.57735,0.57735,-0.57735;2.0944rad)
  LinkedObject = -> <external 105zz_ball_bearing.FCStd>#_05zz_ball_bearing
  Placement = pos=(6,29.35,9.05) rot=(-0.57735,0.57735,-0.57735;2.0944rad)
  expr: Placement = precision_spacer_precision_spacer001.Placement * precision_spacer#LCS_2.Placement * AttachmentOffset * _05zz_ball_bearing#LCS_1.Placement ^ -1
FEATURE [App::Link] micro_v_wheel_micro_v_wheel001
  AssemblyType = Asm4EE
  AttachedBy = #LCS_1
  AttachedTo = _05zz_ball_bearing_105zz_ball_bearing003#LCS_2
  LinkPlacement = pos=(6,34.25,9.05) rot=(0.57735,-0.57735,0.57735;4.18879rad)
  LinkedObject = -> <external micro_v_wheel.FCStd>#delrin_wheel
  Placement = pos=(6,34.25,9.05) rot=(0.57735,-0.57735,0.57735;4.18879rad)
  expr: Placement = _05zz_ball_bearing_105zz_ball_bearing003.Placement * _05zz_ball_bearing#LCS_2.Placement * AttachmentOffset * micro_v_wheel#LCS_1.Placement ^ -1
FEATURE [App::Link] _05zz_ball_bearing_105zz_ball_bearing004
  AssemblyType = Asm4EE
  AttachedBy = #LCS_1
  AttachedTo = micro_v_wheel_micro_v_wheel001#LCS_2
  LinkPlacement = pos=(6,34.35,9.05) rot=(-0.57735,0.57735,-0.57735;2.0944rad)
  LinkedObject = -> <external 105zz_ball_bearing.FCStd>#_05zz_ball_bearing
  Placement = pos=(6,34.35,9.05) rot=(-0.57735,0.57735,-0.57735;2.0944rad)
  expr: Placement = micro_v_wheel_micro_v_wheel001.Placement * micro_v_wheel#LCS_2.Placement * AttachmentOffset * _05zz_ball_bearing#LCS_1.Placement ^ -1
FEATURE [Part::FeaturePython] Screw  label="M5x20-Screw"  # Fasteners workbench fastener (typed FeaturePython)
  AssemblyType = Asm4EE
  AttachedBy = Origin
  AttachedTo = _05zz_ball_bearing_105zz_ball_bearing004#LCS_2
  AttachmentOffset = pos=(0,0,0) rot=(1,0,0;3.14159rad)
  Placement = pos=(6,34.35,9.05) rot=(0.57735,0.57735,0.57735;4.18879rad)
  diameter = 3
  invert = false
  length = 5
  lengthCustom = 20
  matchOuter = false
  offset = 0
  thread = false
  type = 38
  expr: Placement = _05zz_ball_bearing_105zz_ball_bearing004.Placement * _05zz_ball_bearing#LCS_2.Placement * AttachmentOffset
FEATURE [App::Link] silicone_tube_silicone_tube
  AssemblyType = Asm4EE
  AttachedBy = #LCS_1
  AttachedTo = barb_fitting_LC_0640_M6_barb_fitting_LC_0640_M6#LCS_2
  AttachmentOffset = pos=(0,0,0) rot=(0,1,0;3.14159rad)
  LinkPlacement = pos=(21.3,-6.35,5.5) rot=(0,0,1;4.71239rad)
  LinkedObject = -> <external silicone_tube.FCStd>#Part
  Placement = pos=(21.3,-6.35,5.5) rot=(0,0,1;4.71239rad)
  expr: Placement = barb_fitting_LC_0640_M6_barb_fitting_LC_0640_M6.Placement * barb_fitting_LC_0640_M6#LCS_2.Placement * AttachmentOffset * silicone_tube#LCS_1.Placement ^ -1
FEATURE [App::Link] silicone_tube_silicone_tube_2
  AssemblyType = Asm4EE
  AttachedBy = #LCS_1
  AttachedTo = barb_fitting_LC_0640_M6_barb_fitting_LC_0640_M6001#LCS_2
  AttachmentOffset = pos=(0,0,0) rot=(0,-1,0;3.14159rad)
  LinkPlacement = pos=(21.3,6.35,5.5) rot=(0,0,-1;1.5708rad)
  LinkedObject = -> <external silicone_tube.FCStd>#Part
  Placement = pos=(21.3,6.35,5.5) rot=(0,0,-1;1.5708rad)
  expr: Placement = barb_fitting_LC_0640_M6_barb_fitting_LC_0640_M6001.Placement * barb_fitting_LC_0640_M6#LCS_2.Placement * AttachmentOffset * silicone_tube#LCS_1.Placement ^ -1
FEATURE [App::Link] openbuilds_low_profile_screws_low_profile_screw_l25mm
  AssemblyType = Asm4EE
  AttachedBy = #LCS_0
  AttachedTo = watercooled_block_watercooled_block#LCS_1
  AttachmentOffset = pos=(0,0,0) rot=(1,0,0;3.14159rad)
  LinkPlacement = pos=(-9,14.17,40.95) rot=(0,0,1;1.5708rad)
  LinkedObject = -> <external openbuilds_low_profile_screws.FCStd>#low_profile_screw_l25mm
  Placement = pos=(-9,14.17,40.95) rot=(0,0,1;1.5708rad)
  expr: Placement = watercooled_block_watercooled_block.Placement * watercooled_block#LCS_1.Placement * AttachmentOffset * openbuilds_low_profile_screws#LCS_0.Placement ^ -1
FEATURE [App::Link] openbuilds_low_profile_screws_low_profile_screw_l25mm001
  AssemblyType = Asm4EE
  AttachedBy = #LCS_0
  AttachedTo = watercooled_block_watercooled_block#LCS_2
  AttachmentOffset = pos=(0,0,0) rot=(1,0,0;3.14159rad)
  LinkPlacement = pos=(21,14.17,40.95) rot=(0,0,1;1.5708rad)
  LinkedObject = -> <external openbuilds_low_profile_screws.FCStd>#low_profile_screw_l25mm
  Placement = pos=(21,14.17,40.95) rot=(0,0,1;1.5708rad)
  expr: Placement = watercooled_block_watercooled_block.Placement * watercooled_block#LCS_2.Placement * AttachmentOffset * openbuilds_low_profile_screws#LCS_0.Placement ^ -1
FEATURE [PartDesign::CoordinateSystem] LCS_1
  AttacherType = Attacher::AttachEngine3D
  Placement = pos=(6,30,25) rot=(0,0,1;0rad)
FEATURE [App::Link] part_cooling_duct_part_cooling_duct
  LinkPlacement = pos=(26,-16,12) rot=(0,0,1;0rad)
  LinkedObject = -> <external part_cooling_duct.FCStd>#Part
  Placement = pos=(26,-16,12) rot=(0,0,1;0rad)
FEATURE [App::Part] Model
  Configuration = 0
  Group = -> [LCS_Origin,Constraints,Variables,watercooled_block_watercooled_block,barb_fitting_LC_0640_M6_barb_fitting_LC_0640_M6,barb_fitting_LC_0640_M6_barb_fitting_LC_0640_M6001,eccentric_spacer_eccentric_spacer,eccentric_spacer_eccentric_spacer_2,plug_fitting_MSWZ6_plug_fitting_MSWZ6,e3d_volcano_assembly,G5_extruder,precision_spacer_precision_spacer,precision_spacer_precision_spacer_2,+20 more]
  Origin = -> Origin
  Type = Assembly4 Model
---- part x_axis_rail.FCStd = doc fcstd_41f035f62b37 ----
FCSTD DOCUMENT  (FreeCAD 0.19R23578 (Git))
Label: x_axis_rail
License: All rights reserved
LicenseURL: http://en.wikipedia.org/wiki/All_rights_reserved
objects: PartDesign::CoordinateSystem×3, Sketcher::SketchObject×1, PartDesign::Pad×1, PartDesign::Body×1, App::Part×1
note: 7 computed .brp shape members not serialized (recipe doc carries the construction recipe); baked Part::Feature solids carry a one-line shape summary decoded from their .brp

FEATURE [Sketcher::SketchObject] Sketch044
  Placement = pos=(0,0,0) rot=(0,1,0;3.14159rad)
  sketch-geometry (70):
    g0: LineSegment StartX=-3.69 StartY=1.29e-14 StartZ=0 EndX=-3.9 EndY=0.21 EndZ=0
    g1: LineSegment StartX=-3.69 StartY=1.29e-14 StartZ=0 EndX=-3.9 EndY=-0.21 EndZ=0
    g2: LineSegment StartX=-3.9 StartY=-0.21 StartZ=0 EndX=-3.9 EndY=-2.83934 EndZ=0
    g3: LineSegment StartX=-3.9 StartY=-2.83934 StartZ=0 EndX=-6.56066 EndY=-5.5 EndZ=0
    g4: LineSegment StartX=-6.56066 StartY=-5.5 StartZ=0 EndX=-8.2 EndY=-5.5 EndZ=0
    g5: LineSegment StartX=-8.2 StartY=-5.5 StartZ=0 EndX=-8.2 EndY=-3.125 EndZ=0
    g6: LineSegment StartX=-8.2 StartY=-3.125 StartZ=0 EndX=-8.545 EndY=-3.125 EndZ=0
    g7: LineSegment StartX=-8.545 StartY=-3.125 StartZ=0 EndX=-10 EndY=-4.58 EndZ=0
    g8: LineSegment StartX=-10 StartY=-4.58 StartZ=0 EndX=-10 EndY=-9.5 EndZ=0
    g9: ArcOfCircle CenterX=-9.5 CenterY=-9.5 CenterZ=0 NormalX=0 NormalY=0 NormalZ=1 AngleXU=-1e-16 Radius=0.5 StartAngle=3.14159 EndAngle=4.71239
    g10: LineSegment StartX=-9.5 StartY=-10 StartZ=0 EndX=-4.58 EndY=-10 EndZ=0
    g11: LineSegment StartX=-3.125 StartY=-8.545 StartZ=0 EndX=-4.58 EndY=-10 EndZ=0
    g12: LineSegment StartX=-3.125 StartY=-8.2 StartZ=0 EndX=-3.125 EndY=-8.545 EndZ=0
    g13: LineSegment StartX=-5.5 StartY=-8.2 StartZ=0 EndX=-3.125 EndY=-8.2 EndZ=0
    g14: LineSegment StartX=-5.5 StartY=-6.56066 StartZ=0 EndX=-5.5 EndY=-8.2 EndZ=0
    g15: LineSegment StartX=-2.83934 StartY=-3.9 StartZ=0 EndX=-5.5 EndY=-6.56066 EndZ=0
    g16: LineSegment StartX=-0.21 StartY=-3.9 StartZ=0 EndX=-2.83934 EndY=-3.9 EndZ=0
    g17: LineSegment StartX=-4e-16 StartY=-3.69 StartZ=0 EndX=-0.21 EndY=-3.9 EndZ=0
    g18: LineSegment StartX=-4e-16 StartY=-3.69 StartZ=0 EndX=0.21 EndY=-3.9 EndZ=0
    g19: LineSegment StartX=0.21 StartY=-3.9 StartZ=0 EndX=2.83934 EndY=-3.9 EndZ=0
    g20: LineSegment StartX=2.83934 StartY=-3.9 StartZ=0 EndX=5.5 EndY=-6.56066 EndZ=0
    g21: LineSegment StartX=5.5 StartY=-6.56066 StartZ=0 EndX=5.5 EndY=-8.2 EndZ=0
    g22: LineSegment StartX=5.5 StartY=-8.2 StartZ=0 EndX=3.125 EndY=-8.2 EndZ=0
    g23: LineSegment StartX=3.125 StartY=-8.2 StartZ=0 EndX=3.125 EndY=-8.545 EndZ=0
    g24: LineSegment StartX=3.125 StartY=-8.545 StartZ=0 EndX=4.58 EndY=-10 EndZ=0
    g25: LineSegment StartX=4.58 StartY=-10 StartZ=0 EndX=9.5 EndY=-10 EndZ=0
    g26: ArcOfCircle CenterX=9.5 CenterY=-9.5 CenterZ=0 NormalX=0 NormalY=0 NormalZ=1 AngleXU=-1e-16 Radius=0.5 StartAngle=4.71239 EndAngle=6.28319
    g27: LineSegment StartX=10 StartY=-4.58 StartZ=0 EndX=10 EndY=-9.5 EndZ=0
    g28: LineSegment StartX=8.545 StartY=-3.125 StartZ=0 EndX=10 EndY=-4.58 EndZ=0
    g29: LineSegment StartX=8.2 StartY=-3.125 StartZ=0 EndX=8.545 EndY=-3.125 EndZ=0
    g30: LineSegment StartX=8.2 StartY=-5.5 StartZ=0 EndX=8.2 EndY=-3.125 EndZ=0
    g31: LineSegment StartX=6.56066 StartY=-5.5 StartZ=0 EndX=8.2 EndY=-5.5 EndZ=0
    g32: LineSegment StartX=3.9 StartY=-2.83934 StartZ=0 EndX=6.56066 EndY=-5.5 EndZ=0
    g33: LineSegment StartX=3.9 StartY=-0.21 StartZ=0 EndX=3.9 EndY=-2.83934 EndZ=0
    g34: LineSegment StartX=3.69 StartY=1.18e-14 StartZ=0 EndX=3.9 EndY=-0.21 EndZ=0
    g35: LineSegment StartX=3.69 StartY=1.18e-14 StartZ=0 EndX=3.9 EndY=0.21 EndZ=0
    g36: LineSegment StartX=3.9 StartY=0.21 StartZ=0 EndX=3.9 EndY=2.83934 EndZ=0
    g37: LineSegment StartX=3.9 StartY=2.83934 StartZ=0 EndX=6.56066 EndY=5.5 EndZ=0
    g38: LineSegment StartX=6.56066 StartY=5.5 StartZ=0 EndX=8.2 EndY=5.5 EndZ=0
    g39: LineSegment StartX=8.2 StartY=5.5 StartZ=0 EndX=8.2 EndY=3.125 EndZ=0
    g40: LineSegment StartX=8.2 StartY=3.125 StartZ=0 EndX=8.545 EndY=3.125 EndZ=0
    g41: LineSegment StartX=8.545 StartY=3.125 StartZ=0 EndX=10 EndY=4.58 EndZ=0
    g42: LineSegment StartX=10 StartY=9.5 StartZ=0 EndX=10 EndY=4.58 EndZ=0
    g43: ArcOfCircle CenterX=9.5 CenterY=9.5 CenterZ=0 NormalX=0 NormalY=0 NormalZ=1 AngleXU=-1e-16 Radius=0.5 StartAngle=0 EndAngle=1.5708
    g44: LineSegment StartX=4.58 StartY=10 StartZ=0 EndX=9.5 EndY=10 EndZ=0
    g45: LineSegment StartX=3.125 StartY=8.545 StartZ=0 EndX=4.58 EndY=10 EndZ=0
    g46: LineSegment StartX=3.125 StartY=8.2 StartZ=0 EndX=3.125 EndY=8.545 EndZ=0
    g47: LineSegment StartX=5.5 StartY=8.2 StartZ=0 EndX=3.125 EndY=8.2 EndZ=0
    g48: LineSegment StartX=5.5 StartY=6.56066 StartZ=0 EndX=5.5 EndY=8.2 EndZ=0
    g49: LineSegment StartX=2.83934 StartY=3.9 StartZ=0 EndX=5.5 EndY=6.56066 EndZ=0
    g50: LineSegment StartX=0.21 StartY=3.9 StartZ=0 EndX=2.83934 EndY=3.9 EndZ=0
    g51: LineSegment StartX=-2.51e-14 StartY=3.69 StartZ=0 EndX=0.21 EndY=3.9 EndZ=0
    g52: LineSegment StartX=-2.51e-14 StartY=3.69 StartZ=0 EndX=-0.21 EndY=3.9 EndZ=0
    g53: LineSegment StartX=-0.21 StartY=3.9 StartZ=0 EndX=-2.83934 EndY=3.9 EndZ=0
    g54: LineSegment StartX=-2.83934 StartY=3.9 StartZ=0 EndX=-5.5 EndY=6.56066 EndZ=0
    g55: LineSegment StartX=-5.5 StartY=6.56066 StartZ=0 EndX=-5.5 EndY=8.2 EndZ=0
    g56: LineSegment StartX=-5.5 StartY=8.2 StartZ=0 EndX=-3.125 EndY=8.2 EndZ=0
    g57: LineSegment StartX=-3.125 StartY=8.2 StartZ=0 EndX=-3.125 EndY=8.545 EndZ=0
    g58: LineSegment StartX=-3.125 StartY=8.545 StartZ=0 EndX=-4.58 EndY=10 EndZ=0
    g59: LineSegment StartX=-9.5 StartY=10 StartZ=0 EndX=-4.58 EndY=10 EndZ=0
    g60: ArcOfCircle CenterX=-9.5 CenterY=9.5 CenterZ=0 NormalX=0 NormalY=0 NormalZ=1 AngleXU=-1e-16 Radius=0.5 StartAngle=1.5708 EndAngle=3.14159
    g61: LineSegment StartX=-10 StartY=9.5 StartZ=0 EndX=-10 EndY=4.58 EndZ=0
    g62: LineSegment StartX=-8.545 StartY=3.125 StartZ=0 EndX=-10 EndY=4.58 EndZ=0
    g63: LineSegment StartX=-8.2 StartY=3.125 StartZ=0 EndX=-8.545 EndY=3.125 EndZ=0
    g64: LineSegment StartX=-8.2 StartY=5.5 StartZ=0 EndX=-8.2 EndY=3.125 EndZ=0
    g65: LineSegment StartX=-6.56066 StartY=5.5 StartZ=0 EndX=-8.2 EndY=5.5 EndZ=0
    g66: LineSegment StartX=-3.9 StartY=2.83934 StartZ=0 EndX=-6.56066 EndY=5.5 EndZ=0
    g67: LineSegment StartX=-3.9 StartY=0.21 StartZ=0 EndX=-3.9 EndY=2.83934 EndZ=0
    g68: ArcOfCircle CenterX=0 CenterY=0 CenterZ=0 NormalX=0 NormalY=0 NormalZ=1 AngleXU=-1e-16 Radius=2.1 StartAngle=3.14159 EndAngle=6.28319
    g69: ArcOfCircle CenterX=0 CenterY=0 CenterZ=0 NormalX=0 NormalY=0 NormalZ=1 AngleXU=-1e-16 Radius=2.1 StartAngle=0 EndAngle=3.14159
  constraints (149):
    c: Coincident(g0,g1)
    c: Coincident(g1,g2)
    c: Coincident(g2,g3)
    c: Coincident(g3,g4)
    c: Coincident(g4,g5)
    c: Coincident(g5,g6)
    c: Coincident(g6,g7)
    c: Coincident(g7,g8)
    c: Coincident(g8,g9)
    c: Coincident(g9,g10)
    c: Coincident(g10,g11)
    c: Coincident(g11,g12)
    c: Vertical(g12)
    c: Coincident(g12,g13)
    c: Horizontal(g13)
    c: Coincident(g13,g14)
    c: Vertical(g14)
    c: Coincident(g14,g15)
    c: Coincident(g15,g16)
    c: Coincident(g16,g17)
    c: Coincident(g17,g18)
    c: Coincident(g18,g19)
    c: Horizontal(g19)
    c: Coincident(g19,g20)
    c: Coincident(g20,g21)
    c: Vertical(g21)
    c: Coincident(g21,g22)
    c: Horizontal(g22)
    c: Coincident(g22,g23)
    c: Vertical(g23)
    c: Coincident(g23,g24)
    c: Coincident(g24,g25)
    c: Coincident(g25,g26)
    c: Coincident(g26,g27)
    c: Coincident(g27,g28)
    c: Coincident(g28,g29)
    c: Coincident(g29,g30)
    c: Coincident(g30,g31)
    c: Coincident(g31,g32)
    c: Coincident(g32,g33)
    c: Coincident(g33,g34)
    c: Coincident(g34,g35)
    c: Coincident(g35,g36)
    c: Coincident(g36,g37)
    c: Coincident(g37,g38)
    c: Coincident(g38,g39)
    c: Coincident(g39,g40)
    c: Coincident(g40,g41)
    c: Coincident(g41,g42)
    c: Coincident(g42,g43)
    c: Coincident(g43,g44)
    c: Horizontal(g44)
    c: Coincident(g44,g45)
    c: Coincident(g45,g46)
    c: Coincident(g46,g47)
    c: Coincident(g47,g48)
    c: Coincident(g48,g49)
    c: Coincident(g49,g50)
    c: Coincident(g50,g51)
    c: Coincident(g51,g52)
    c: Coincident(g52,g53)
    c: Coincident(g53,g54)
    c: Coincident(g54,g55)
    c: Coincident(g55,g56)
    c: Coincident(g56,g57)
    c: Coincident(g57,g58)
    c: Coincident(g58,g59)
    c: Horizontal(g59)
    c: Coincident(g59,g60)
    c: Coincident(g60,g61)
    c: Coincident(g61,g62)
    c: Coincident(g62,g63)
    c: Coincident(g63,g64)
    c: Coincident(g64,g65)
    c: Coincident(g65,g66)
    c: Coincident(g66,g67)
    c: Coincident(g67,g0)
    c: Coincident(g68,g69)
    c: Coincident(g69,g68)
    c: Block(g30)
    c: Block(g29)
    c: Block(g28)
    c: Block(g27)
    c: Block(g31)
    c: Block(g32)
    c: Block(g33)
    c: Block(g34)
    c: Block(g35)
    c: Block(g36)
    c: Block(g69)
    c: Block(g68)
    c: Block(g37)
    c: Block(g38)
    c: Block(g39)
    c: Block(g40)
    c: Block(g41)
    c: Block(g42)
    c: Block(g43)
    c: Block(g44)
    c: Block(g45)
    c: Block(g46)
    c: Block(g47)
    c: Block(g48)
    c: Block(g49)
    c: Block(g50)
    c: Block(g53)
    c: Block(g52)
    c: Block(g51)
    c: Block(g54)
    c: Block(g55)
    c: Block(g56)
    c: Block(g57)
    c: Block(g58)
    c: Block(g59)
    c: Block(g60)
    c: Block(g61)
    c: Block(g62)
    c: Block(g63)
    c: Block(g64)
    c: Block(g65)
    c: Block(g66)
    c: Block(g67)
    c: Block(g0)
    c: Block(g1)
    c: Block(g2)
    c: Block(g3)
    c: Block(g4)
    c: Block(g5)
    c: Block(g6)
    c: Block(g7)
    c: Block(g8)
    c: Block(g9)
    c: Block(g10)
    c: Block(g11)
    c: Block(g12)
    c: Block(g13)
    c: Block(g14)
    c: Block(g15)
    c: Block(g16)
    c: Block(g17)
    c: Block(g18)
    c: Block(g19)
    c: Block(g20)
    c: Block(g21)
    c: Block(g22)
    c: Block(g23)
    c: Block(g24)
    c: Block(g25)
    c: Block(g26)
FEATURE [PartDesign::Pad] Pad018
  AllowMultiFace = false
  Direction = (1,1,1)
  Length = 380
  Length2 = 100
  Placement = pos=(0,0,0) rot=(0,1,0;3.14159rad)
  Profile = -> Sketch044
  Reversed = true
  Type = 0
FEATURE [PartDesign::Body] Body017  label="Body"
  Group = -> [Sketch044,Pad018]
  Origin = -> Origin047
  Tip = -> Pad018
FEATURE [PartDesign::CoordinateSystem] LCS_1
  AttacherType = Attacher::AttachEngine3D
  MapMode = 45
  Placement = pos=(1e-16,-1e-16,380) rot=(0,0,1;0rad)
  Support = -> [Pad018]
FEATURE [PartDesign::CoordinateSystem] LCS_2
  AttacherType = Attacher::AttachEngine3D
  MapMode = 45
  Placement = pos=(-10,-3.9e-14,0) rot=(0,0.707107,0.707107;3.14159rad)
  Support = -> [Pad018]
FEATURE [PartDesign::CoordinateSystem] LCS_3
  AttacherType = Attacher::AttachEngine3D
  MapMode = 45
  Placement = pos=(1e-16,-1e-16,190) rot=(0,0,1;0rad)
  Support = -> [Pad018]
FEATURE [App::Part] Part028  label="2020_vslot_rail"
  Group = -> [Body017,LCS_1,LCS_2,LCS_3]
  Origin = -> Origin042
---- part x_idler_bracket.FCStd = doc fcstd_dfdd957a001c ----
FCSTD DOCUMENT  (FreeCAD 0.19R23578 (Git))
Label: x_idler_bracket
License: All rights reserved
LicenseURL: http://en.wikipedia.org/wiki/All_rights_reserved
objects: TechDraw::DrawViewDimension×16, Sketcher::SketchObject×4, PartDesign::Pocket×3, TechDraw::DrawProjGroupItem×3, PartDesign::CoordinateSystem×2, PartDesign::Pad×1, PartDesign::Body×1, TechDraw::DrawSVGTemplate×1, App::Part×1, TechDraw::DrawViewPart×1, TechDraw::DrawProjGroup×1, TechDraw::DrawPage×1
note: 15 computed .brp shape members not serialized (recipe doc carries the construction recipe); baked Part::Feature solids carry a one-line shape summary decoded from their .brp

FEATURE [Sketcher::SketchObject] Sketch047
  MapMode = 5
  Support = -> [XY_Plane060]
  sketch-geometry (6):
    g0: ArcOfCircle CenterX=11 CenterY=-14 CenterZ=0 NormalX=0 NormalY=0 NormalZ=1 AngleXU=0 Radius=6.5 StartAngle=3.57338 EndAngle=6.89834
    g1: LineSegment StartX=0 StartY=-10 StartZ=0 EndX=0 EndY=10 EndZ=0
    g2: LineSegment StartX=0 StartY=10 StartZ=0 EndX=2 EndY=10 EndZ=0
    g3: LineSegment StartX=2 StartY=10 StartZ=0 EndX=16.3084 EndY=-10.2489 EndZ=0
    g4: LineSegment StartX=0 StartY=-10 StartZ=0 EndX=2 EndY=-10 EndZ=0
    g5: LineSegment StartX=2 StartY=-10 StartZ=0 EndX=5.09658 EndY=-16.7202 EndZ=0
  constraints (18):
    c: Vertical(g1)
    c: Coincident(g1,g2)
    c: Horizontal(g2)
    c: Coincident(g2,g3)
    c: Diameter(g0) = 13
    c: PointOnObject(g-1,g1)
    c: DistanceY(g-1,g1) = 10
    c: DistanceY(g1,g-1) = 10
    c: DistanceX(g2,g2) = 2
    c: DistanceX(g-1,g0) = 11
    c: DistanceY(g0,g-1) = 14
    c: Coincident(g1,g4)
    c: Coincident(g4,g5)
    c: Tangent(g5,g0)
    c: DistanceX(g4,g4) = 2
    c: Coincident(g5,g0)
    c: Horizontal(g4)
    c: Tangent(g3,g0) = 1.5708
FEATURE [PartDesign::Pad] Pad020  label="Pad021"
  AllowMultiFace = false
  Direction = (1,1,1)
  Length = 20
  Length2 = 100
  Midplane = true
  Profile = -> Sketch047
  Type = 0
FEATURE [Sketcher::SketchObject] Sketch048
  MapMode = 5
  Placement = pos=(0,0,0) rot=(0.57735,0.57735,0.57735;2.0944rad)
  Support = -> [YZ_Plane060]
  sketch-geometry (5):
    g0: LineSegment StartX=-24 StartY=6.1 StartZ=0 EndX=-4 EndY=6.1 EndZ=0
    g1: LineSegment StartX=-4 StartY=6.1 StartZ=0 EndX=-4 EndY=-6.1 EndZ=0
    g2: LineSegment StartX=-4 StartY=-6.1 StartZ=0 EndX=-24 EndY=-6.1 EndZ=0
    g3: LineSegment StartX=-24 StartY=-6.1 StartZ=0 EndX=-24 EndY=6.1 EndZ=0
    g4: Circle CenterX=0 CenterY=0 CenterZ=0 NormalX=0 NormalY=0 NormalZ=1 AngleXU=0 Radius=2.55
  constraints (12):
    c: Coincident(g0,g1)
    c: Coincident(g1,g2)
    c: Coincident(g2,g3)
    c: Coincident(g3,g0)
    c: Horizontal(g0)
    c: Symmetric(g2,g0,g-1)
    c: Symmetric(g0,g1,g-1)
    c: DistanceX(g0,g0) = 20
    c: DistanceY(g3,g3) = 12.2
    c: Coincident(g4,g-1)
    c: Diameter(g4) = 5.1
    c: DistanceX(g0,g4) = 4
FEATURE [Sketcher::SketchObject] Sketch049
  AttachmentOffset = pos=(0,0,4) rot=(0,0,1;0rad)
  MapMode = 5
  Placement = pos=(4,-9e-16,9e-16) rot=(0.57735,0.57735,0.57735;2.0944rad)
  Support = -> [YZ_Plane060]
  sketch-geometry (4):
    g0: LineSegment StartX=-25 StartY=6.1 StartZ=0 EndX=25 EndY=6.1 EndZ=0
    g1: LineSegment StartX=25 StartY=6.1 StartZ=0 EndX=25 EndY=-6.1 EndZ=0
    g2: LineSegment StartX=25 StartY=-6.1 StartZ=0 EndX=-25 EndY=-6.1 EndZ=0
    g3: LineSegment StartX=-25 StartY=-6.1 StartZ=0 EndX=-25 EndY=6.1 EndZ=0
  constraints (12):
    c: Coincident(g0,g1)
    c: Coincident(g1,g2)
    c: Coincident(g2,g3)
    c: Coincident(g3,g0)
    c: Horizontal(g0)
    c: Horizontal(g2)
    c: Vertical(g1)
    c: Vertical(g3)
    c: DistanceX(g0,g0) = 50
    c: DistanceX(g-1,g0) = 25
    c: DistanceY(g-1,g0) = 6.1
    c: DistanceY(g1,g1) = 12.2
FEATURE [PartDesign::Pocket] Pocket016
  AllowMultiFace = false
  BaseFeature = -> Pad020
  Length = 5
  Length2 = 100
  Midplane = true
  Profile = -> Sketch048
  Type = 1
FEATURE [PartDesign::Pocket] Pocket017
  AllowMultiFace = false
  BaseFeature = -> Pocket016
  Length = 5
  Length2 = 100
  Profile = -> Sketch049
  Reversed = true
  Type = 1
FEATURE [Sketcher::SketchObject] Sketch050
  MapMode = 5
  Support = -> [XY_Plane060]
  sketch-geometry (1):
    g0: Circle CenterX=11 CenterY=-14 CenterZ=0 NormalX=0 NormalY=0 NormalZ=1 AngleXU=0 Radius=2.5
  constraints (3):
    c: DistanceY(g0,g-1) = 14
    c: DistanceX(g-1,g0) = 11
    c: Diameter(g0) = 5
FEATURE [PartDesign::Pocket] Pocket018
  AllowMultiFace = false
  BaseFeature = -> Pocket017
  Length = 5
  Length2 = 100
  Midplane = true
  Profile = -> Sketch050
  Type = 1
FEATURE [PartDesign::Body] Body020
  Group = -> [Sketch047,Pad020,Sketch048,Sketch049,Pocket016,Pocket017,Sketch050,Pocket018]
  Origin = -> Origin060
  Tip = -> Pocket018
FEATURE [TechDraw::DrawSVGTemplate] Template004
  EditableTexts = Author=Alex Neufeld; DWG_num=2020-103; Date=15/05/2020; Revision=2; Scale=NTS; Subtitle=For use with 20T 2GT pulley; Title=X-Axis Idler Bracket
  Height = 215.9
  Orientation = 1
  Width = 279.4
FEATURE [PartDesign::CoordinateSystem] LCS_1
  AttacherType = Attacher::AttachEngine3D
  MapMode = 11
  Placement = pos=(0,0,2.776e-13) rot=(0.707107,0,0.707107;3.14159rad)
  Support = -> [Pocket018]
FEATURE [PartDesign::CoordinateSystem] LCS_2
  AttacherType = Attacher::AttachEngine3D
  MapMode = 45
  Placement = pos=(11,-14,0) rot=(0.57735,0.57735,0.57735;2.0944rad)
  Support = -> [Pocket018]
FEATURE [App::Part] Part033  label="x_idler_bracket"
  Group = -> [Body020,LCS_1,LCS_2]
  Origin = -> Origin051
FEATURE [TechDraw::DrawViewPart] View004
  CoarseView = false
  Direction = (0.577,-0.577,0.577)
  Focus = 100
  HardHidden = false
  IsoCount = 0
  IsoHidden = false
  IsoVisible = false
  LockPosition = true
  Perspective = false
  Rotation = 0
  ScaleType = 0
  SeamHidden = false
  SeamVisible = true
  SmoothHidden = false
  SmoothVisible = true
  Source = -> [Part033]
  X = 36.0346
  XDirection = (0.707,0.707,0)
  Y = 180.306
FEATURE [TechDraw::DrawProjGroupItem] ProjItem017  label="Front004"
  CoarseView = false
  Direction = (1,0,0)
  Focus = 100
  HardHidden = false
  IsoCount = 0
  IsoHidden = false
  IsoVisible = false
  LockPosition = true
  Perspective = false
  Rotation = 0
  RotationVector = (0,1,0)
  Scale = 2
  ScaleType = 2
  SeamHidden = false
  SeamVisible = true
  SmoothHidden = false
  SmoothVisible = true
  Source = -> [View004,Part033]
  Type = 0
  X = 0
  XDirection = (0,-1,1e-16)
  Y = 0
FEATURE [TechDraw::DrawProjGroupItem] ProjItem018  label="Bottom004"
  CoarseView = false
  Direction = (0,1e-16,1)
  Focus = 100
  HardHidden = false
  IsoCount = 0
  IsoHidden = false
  IsoVisible = false
  LockPosition = true
  Perspective = false
  Rotation = 0
  RotationVector = (1,0,0)
  Scale = 2
  ScaleType = 2
  SeamHidden = false
  SeamVisible = true
  SmoothHidden = false
  SmoothVisible = true
  Source = -> [View004,Part033]
  Type = 5
  X = 0
  XDirection = (0,-1,1e-16)
  Y = 64.4821
FEATURE [TechDraw::DrawProjGroupItem] ProjItem019  label="Left003"
  CoarseView = false
  Direction = (1e-16,1,-1e-16)
  Focus = 100
  HardHidden = false
  IsoCount = 0
  IsoHidden = false
  IsoVisible = false
  LockPosition = true
  Perspective = false
  Rotation = 0
  RotationVector = (1,0,0)
  Scale = 2
  ScaleType = 2
  SeamHidden = false
  SeamVisible = true
  SmoothHidden = false
  SmoothVisible = true
  Source = -> [View004,Part033]
  Type = 1
  X = 76
  XDirection = (1,-1e-16,0)
  Y = 0
FEATURE [TechDraw::DrawProjGroup] ProjGroup004
  Anchor = -> ProjItem017
  AutoDistribute = true
  LockPosition = false
  ProjectionType = 0
  Rotation = 0
  Scale = 2
  ScaleType = 2
  Source = -> [View004,Part033]
  Views = -> [ProjItem017,ProjItem018,ProjItem019]
  X = 118.879
  Y = 93.5714
  spacingX = 15
  spacingY = 15
FEATURE [TechDraw::DrawViewDimension] Dimension082
  Arbitrary = false
  ArbitraryTolerances = false
  FormatSpec = %.2f
  FormatSpecOverTolerance = %+.2f
  FormatSpecUnderTolerance = %+.2f
  Inverted = false
  LockPosition = false
  MeasureType = 1
  OverTolerance = 0
  References2D = -> [ProjItem018]
  Rotation = 0
  ScaleType = 0
  TheoreticalExact = false
  Type = 2
  UnderTolerance = 0
  X = -38.4355
  Y = -15.5
FEATURE [TechDraw::DrawViewDimension] Dimension083
  Arbitrary = false
  ArbitraryTolerances = false
  FormatSpec = %.2f
  FormatSpecOverTolerance = %+.2f
  FormatSpecUnderTolerance = %+.2f
  Inverted = false
  LockPosition = false
  MeasureType = 1
  OverTolerance = 0
  References2D = -> [ProjItem018]
  Rotation = 0
  ScaleType = 0
  TheoreticalExact = false
  Type = 2
  UnderTolerance = 0
  X = 37.4428
  Y = -7.00652
FEATURE [TechDraw::DrawViewDimension] Dimension084
  Arbitrary = false
  ArbitraryTolerances = false
  FormatSpec = %.2f
  FormatSpecOverTolerance = %+.2f
  FormatSpecUnderTolerance = %+.2f
  Inverted = false
  LockPosition = false
  MeasureType = 1
  OverTolerance = 0
  References2D = -> [ProjItem018]
  Rotation = 0
  ScaleType = 0
  TheoreticalExact = false
  Type = 1
  UnderTolerance = 0
  X = -8.18841
  Y = 28.9239
FEATURE [TechDraw::DrawViewDimension] Dimension085
  Arbitrary = false
  ArbitraryTolerances = false
  FormatSpec = R%.2f
  FormatSpecOverTolerance = %+.2f
  FormatSpecUnderTolerance = %+.2f
  Inverted = false
  LockPosition = false
  MeasureType = 1
  OverTolerance = 0
  References2D = -> [ProjItem018]
  Rotation = 0
  ScaleType = 0
  TheoreticalExact = false
  Type = 4
  UnderTolerance = 0
  X = 38.8334
  Y = 18.066
FEATURE [TechDraw::DrawViewDimension] Dimension086
  Arbitrary = false
  ArbitraryTolerances = false
  FormatSpec = ⌀%.2f
  FormatSpecOverTolerance = %+.2f
  FormatSpecUnderTolerance = %+.2f
  Inverted = false
  LockPosition = false
  MeasureType = 1
  OverTolerance = 0
  References2D = -> [ProjItem018]
  Rotation = 0
  ScaleType = 0
  TheoreticalExact = false
  Type = 5
  UnderTolerance = 0
  X = 6.07827
  Y = -4.13322
FEATURE [TechDraw::DrawViewDimension] Dimension087
  Arbitrary = false
  ArbitraryTolerances = false
  FormatSpec = %.2f
  FormatSpecOverTolerance = %+.2f
  FormatSpecUnderTolerance = %+.2f
  Inverted = false
  LockPosition = false
  MeasureType = 1
  OverTolerance = 0
  References2D = -> [ProjItem018]
  Rotation = 0
  ScaleType = 0
  TheoreticalExact = false
  Type = 1
  UnderTolerance = 0
  X = -10.1623
  Y = -23.4094
FEATURE [TechDraw::DrawViewDimension] Dimension088
  Arbitrary = false
  ArbitraryTolerances = false
  FormatSpec = %.2f
  FormatSpecOverTolerance = %+.2f
  FormatSpecUnderTolerance = %+.2f
  Inverted = false
  LockPosition = false
  MeasureType = 1
  OverTolerance = 0
  References2D = -> [ProjItem018]
  Rotation = 0
  ScaleType = 0
  TheoreticalExact = false
  Type = 6
  UnderTolerance = 0
  X = -8.44204
  Y = -7.93551
FEATURE [TechDraw::DrawViewDimension] Dimension089
  Arbitrary = false
  ArbitraryTolerances = false
  FormatSpec = %.2f
  FormatSpecOverTolerance = %+.2f
  FormatSpecUnderTolerance = %+.2f
  Inverted = false
  LockPosition = false
  MeasureType = 1
  OverTolerance = 0
  References2D = -> [ProjItem017]
  Rotation = 0
  ScaleType = 0
  TheoreticalExact = false
  Type = 1
  UnderTolerance = 0
  X = -20.2974
  Y = 25.9805
FEATURE [TechDraw::DrawViewDimension] Dimension090
  Arbitrary = false
  ArbitraryTolerances = false
  FormatSpec = %.2f
  FormatSpecOverTolerance = %+.2f
  FormatSpecUnderTolerance = %+.2f
  Inverted = false
  LockPosition = false
  MeasureType = 1
  OverTolerance = 0
  References2D = -> [ProjItem017]
  Rotation = 0
  ScaleType = 0
  TheoreticalExact = false
  Type = 2
  UnderTolerance = 0
  X = -45.5396
  Y = -8.78435
FEATURE [TechDraw::DrawViewDimension] Dimension091
  Arbitrary = false
  ArbitraryTolerances = false
  FormatSpec = %.2f
  FormatSpecOverTolerance = %+.2f
  FormatSpecUnderTolerance = %+.2f
  Inverted = false
  LockPosition = false
  MeasureType = 1
  OverTolerance = 0
  References2D = -> [ProjItem017]
  Rotation = 0
  ScaleType = 0
  TheoreticalExact = false
  Type = 1
  UnderTolerance = 0
  X = 1.01304
  Y = -29.1174
FEATURE [TechDraw::DrawViewDimension] Dimension092
  Arbitrary = false
  ArbitraryTolerances = false
  FormatSpec = %.2f
  FormatSpecOverTolerance = %+.2f
  FormatSpecUnderTolerance = %+.2f
  Inverted = false
  LockPosition = false
  MeasureType = 1
  OverTolerance = 0
  References2D = -> [ProjItem017]
  Rotation = 0
  ScaleType = 0
  TheoreticalExact = false
  Type = 2
  UnderTolerance = 0
  X = -52.8948
  Y = -0.11725
FEATURE [TechDraw::DrawViewDimension] Dimension093
  Arbitrary = false
  ArbitraryTolerances = false
  FormatSpec = %.2f
  FormatSpecOverTolerance = %+.2f
  FormatSpecUnderTolerance = %+.2f
  Inverted = false
  LockPosition = false
  MeasureType = 1
  OverTolerance = 0
  References2D = -> [ProjItem019]
  Rotation = 0
  ScaleType = 0
  TheoreticalExact = false
  Type = 1
  UnderTolerance = 0
  X = -0.330424
  Y = -36.192
FEATURE [TechDraw::DrawViewDimension] Dimension094
  Arbitrary = false
  ArbitraryTolerances = false
  FormatSpec = %.2f
  FormatSpecOverTolerance = %+.2f
  FormatSpecUnderTolerance = %+.2f
  Inverted = false
  LockPosition = false
  MeasureType = 1
  OverTolerance = 0
  References2D = -> [ProjItem019]
  Rotation = 0
  ScaleType = 0
  TheoreticalExact = false
  Type = 1
  UnderTolerance = 0
  X = -1.85725
  Y = 28.1044
FEATURE [TechDraw::DrawViewDimension] Dimension095
  Arbitrary = false
  ArbitraryTolerances = false
  FormatSpec = %.2f
  FormatSpecOverTolerance = %+.2f
  FormatSpecUnderTolerance = %+.2f
  Inverted = false
  LockPosition = false
  MeasureType = 1
  OverTolerance = 0
  References2D = -> [ProjItem019]
  Rotation = 0
  ScaleType = 0
  TheoreticalExact = false
  Type = 2
  UnderTolerance = 0
  X = 23.4094
  Y = 0.506522
FEATURE [TechDraw::DrawViewDimension] Dimension096
  Arbitrary = false
  ArbitraryTolerances = false
  FormatSpec = %.2f
  FormatSpecOverTolerance = %+.2f
  FormatSpecUnderTolerance = %+.2f
  Inverted = false
  LockPosition = false
  MeasureType = 1
  OverTolerance = 0
  References2D = -> [ProjItem017]
  Rotation = 0
  ScaleType = 0
  TheoreticalExact = false
  Type = 1
  UnderTolerance = 0
  X = 13.6623
  Y = -1.05651
FEATURE [TechDraw::DrawViewDimension] Dimension097
  Arbitrary = false
  ArbitraryTolerances = false
  FormatSpec = ⌀%.2f
  FormatSpecOverTolerance = %+.2f
  FormatSpecUnderTolerance = %+.2f
  Inverted = false
  LockPosition = false
  MeasureType = 1
  OverTolerance = 0
  References2D = -> [ProjItem017]
  Rotation = 0
  ScaleType = 0
  TheoreticalExact = false
  Type = 5
  UnderTolerance = 0
  X = 4.37635
  Y = 6.07827
FEATURE [TechDraw::DrawPage] Page004  label="x_idler_bracket_dwg001"
  KeepUpdated = false
  NextBalloonIndex = 1
  ProjectionType = 0
  Template = -> Template004
  Views = -> [View004,ProjGroup004,Dimension082,Dimension083,Dimension084,Dimension085,Dimension086,Dimension087,Dimension088,Dimension089,Dimension090,Dimension091,Dimension092,Dimension093,Dimension094,Dimension095,Dimension096,Dimension097]
---- part y_axis_carriage_block.FCStd = doc fcstd_7cf693d7afa6 ----
FCSTD DOCUMENT  (FreeCAD 0.19R23578 (Git))
Label: y_axis_carriage_block
License: All rights reserved
LicenseURL: http://en.wikipedia.org/wiki/All_rights_reserved
objects: TechDraw::DrawViewDimension×41, PartDesign::CoordinateSystem×15, Sketcher::SketchObject×10, PartDesign::Pocket×6, TechDraw::DrawProjGroupItem×3, TechDraw::DrawViewDimExtent×3, PartDesign::Pad×2, PartDesign::Fillet×2, PartDesign::Hole×2, TechDraw::DrawSVGTemplate×1, PartDesign::Body×1, TechDraw::DrawViewAnnotation×1, App::Part×1, TechDraw::DrawViewPart×1, TechDraw::DrawProjGroup×1, TechDraw::DrawViewDetail×1, TechDraw::DrawLeaderLine×1, TechDraw::DrawPage×1
note: 50 computed .brp shape members not serialized (recipe doc carries the construction recipe); baked Part::Feature solids carry a one-line shape summary decoded from their .brp

FEATURE [Sketcher::SketchObject] Sketch037
  MapMode = 5
  Support = -> [XY_Plane046]
  sketch-geometry (4):
    g0: LineSegment StartX=0 StartY=50 StartZ=0 EndX=6.35 EndY=50 EndZ=0
    g1: LineSegment StartX=6.35 StartY=50 StartZ=0 EndX=6.35 EndY=-50 EndZ=0
    g2: LineSegment StartX=6.35 StartY=-50 StartZ=0 EndX=0 EndY=-50 EndZ=0
    g3: LineSegment StartX=0 StartY=-50 StartZ=0 EndX=0 EndY=50 EndZ=0
  constraints (11):
    c: Coincident(g0,g1)
    c: Coincident(g1,g2)
    c: Coincident(g2,g3)
    c: Coincident(g3,g0)
    c: Horizontal(g0)
    c: Horizontal(g2)
    c: Vertical(g1)
    c: PointOnObject(g0,g-2)
    c: Symmetric(g2,g0,g-1)
    c: DistanceY(g2,g0) = 100
    c: DistanceX(g0,g0) = 6.35
FEATURE [PartDesign::Pad] Pad016
  AllowMultiFace = false
  Direction = (1,1,1)
  Length = 120
  Length2 = 100
  Midplane = true
  Profile = -> Sketch037
  Type = 0
FEATURE [Sketcher::SketchObject] Sketch038
  AttachmentOffset = pos=(0,0,6.35) rot=(0,0,1;0rad)
  MapMode = 5
  Placement = pos=(6.35,-1.4e-15,1.4e-15) rot=(0.57735,0.57735,0.57735;2.0944rad)
  Support = -> [YZ_Plane046]
  sketch-geometry (20):
    g0: LineSegment StartX=4 StartY=60 StartZ=0 EndX=4 EndY=10 EndZ=0
    g1: LineSegment StartX=4 StartY=10 StartZ=0 EndX=0 EndY=10 EndZ=0
    g2: LineSegment StartX=0 StartY=10 StartZ=0 EndX=0 EndY=4.5 EndZ=0
    g3: LineSegment StartX=0 StartY=4.5 StartZ=0 EndX=-1 EndY=3.5 EndZ=0
    g4: LineSegment StartX=-1 StartY=3.5 StartZ=0 EndX=-1 EndY=3 EndZ=0
    g5: LineSegment StartX=-1 StartY=3 StartZ=0 EndX=0 EndY=3 EndZ=0
    g6: LineSegment StartX=0 StartY=3 StartZ=0 EndX=0 EndY=-3 EndZ=0
    g7: LineSegment StartX=0 StartY=-3 StartZ=0 EndX=-1 EndY=-3 EndZ=0
    g8: LineSegment StartX=-1 StartY=-3 StartZ=0 EndX=-1 EndY=-3.5 EndZ=0
    g9: LineSegment StartX=-1 StartY=-3.5 StartZ=0 EndX=0 EndY=-4.5 EndZ=0
    g10: LineSegment StartX=0 StartY=-4.5 StartZ=0 EndX=0 EndY=-10 EndZ=0
    g11: LineSegment StartX=0 StartY=-10 StartZ=0 EndX=4 EndY=-10 EndZ=0
    g12: LineSegment StartX=4 StartY=-10 StartZ=0 EndX=4 EndY=-60 EndZ=0
    g13: LineSegment StartX=4 StartY=-60 StartZ=0 EndX=8 EndY=-60 EndZ=0
    g14: LineSegment StartX=8 StartY=-60 StartZ=0 EndX=8 EndY=-10 EndZ=0
    g15: LineSegment StartX=8 StartY=-10 StartZ=0 EndX=50 EndY=-10 EndZ=0
    g16: LineSegment StartX=50 StartY=-10 StartZ=0 EndX=50 EndY=-6 EndZ=0
    g17: LineSegment StartX=50 StartY=-6 StartZ=0 EndX=8 EndY=-6 EndZ=0
    g18: LineSegment StartX=8 StartY=-6 StartZ=0 EndX=8 EndY=60 EndZ=0
    g19: LineSegment StartX=8 StartY=60 StartZ=0 EndX=4 EndY=60 EndZ=0
  constraints (56):
    c: Vertical(g0)
    c: Coincident(g0,g1)
    c: Horizontal(g1)
    c: Coincident(g1,g2)
    c: Vertical(g2)
    c: Coincident(g2,g3)
    c: Coincident(g3,g4)
    c: Coincident(g4,g5)
    c: Horizontal(g5)
    c: Coincident(g5,g6)
    c: Coincident(g6,g7)
    c: Coincident(g7,g8)
    c: Coincident(g8,g9)
    c: Coincident(g9,g10)
    c: Vertical(g10)
    c: Coincident(g10,g11)
    c: Coincident(g11,g12)
    c: Vertical(g12)
    c: Coincident(g12,g13)
    c: Horizontal(g13)
    c: Coincident(g13,g14)
    c: Vertical(g14)
    c: Coincident(g14,g15)
    c: Horizontal(g15)
    c: Coincident(g15,g16)
    c: Coincident(g16,g17)
    c: Horizontal(g17)
    c: Coincident(g17,g18)
    c: Vertical(g18)
    c: Coincident(g18,g19)
    c: Coincident(g19,g0)
    c: Vertical(g4)
    c: Vertical(g6)
    c: Vertical(g16)
    c: Horizontal(g19)
    c: Horizontal(g7)
    c: Horizontal(g11)
    c: Vertical(g17,g14)
    c: Angle(g5,g3) = 0.785398
    c: Angle(g9,g7) = 0.785398
    c: DistanceY(g8,g8) = 0.5
    c: DistanceY(g6,g6) = 6
    c: Symmetric(g10,g1,g-1)
    c: Vertical(g9,g6)
    c: Symmetric(g7,g4,g-1)
    c: PointOnObject(g-1,g6)
    c: Symmetric(g3,g8,g-1)
    c: DistanceY(g-1,g2) = 4.5
    c: DistanceX(g1,g1) = 4
    c: Symmetric(g12,g0,g-1)
    c: DistanceY(g-1,g18) = 60
    c: DistanceX(g19,g19) = 4
    c: DistanceX(g-1,g15) = 50
    c: DistanceY(g-1,g0) = 10
    c: DistanceY(g16,g16) = 4
    c: Horizontal(g14,g11)
FEATURE [PartDesign::Pad] Pad017
  AllowMultiFace = false
  BaseFeature = -> Pad016
  Direction = (1,1,1)
  Length = 120
  Length2 = 100
  Profile = -> Sketch038
  Type = 0
FEATURE [Sketcher::SketchObject] Sketch039
  MapMode = 5
  Placement = pos=(0,0,0) rot=(1,0,0;1.5708rad)
  Support = -> [XZ_Plane046]
  sketch-geometry (6):
    g0: LineSegment StartX=16.35 StartY=60 StartZ=0 EndX=126.35 EndY=10 EndZ=0
    g1: LineSegment StartX=126.35 StartY=10 StartZ=0 EndX=126.35 EndY=60 EndZ=0
    g2: LineSegment StartX=126.35 StartY=60 StartZ=0 EndX=16.35 EndY=60 EndZ=0
    g3: LineSegment StartX=16.35 StartY=-60 StartZ=0 EndX=126.35 EndY=-10 EndZ=0
    g4: LineSegment StartX=126.35 StartY=-10 StartZ=0 EndX=126.35 EndY=-60 EndZ=0
    g5: LineSegment StartX=126.35 StartY=-60 StartZ=0 EndX=16.35 EndY=-60 EndZ=0
  constraints (15):
    c: Coincident(g0,g1)
    c: Coincident(g1,g2)
    c: Coincident(g2,g0)
    c: Horizontal(g2)
    c: Coincident(g3,g4)
    c: Coincident(g4,g5)
    c: Coincident(g5,g3)
    c: Symmetric(g3,g0,g-1)
    c: Symmetric(g3,g0,g-1)
    c: Symmetric(g1,g4,g-1)
    c: Vertical(g1)
    c: DistanceY(g-1,g0) = 60
    c: DistanceX(g-1,g1) = 126.35
    c: DistanceX(g-1,g0) = 16.35
    c: DistanceY(g-1,g0) = 10
FEATURE [PartDesign::Pocket] Pocket013
  AllowMultiFace = false
  BaseFeature = -> Pad017
  Length = 5
  Length2 = 100
  Midplane = true
  Profile = -> Sketch039
  Type = 1
FEATURE [Sketcher::SketchObject] Sketch040
  MapMode = 5
  Support = -> [XY_Plane046]
  sketch-geometry (3):
    g0: LineSegment StartX=16.35 StartY=50 StartZ=0 EndX=126.35 EndY=10 EndZ=0
    g1: LineSegment StartX=126.35 StartY=50 StartZ=0 EndX=126.35 EndY=10 EndZ=0
    g2: LineSegment StartX=126.35 StartY=50 StartZ=0 EndX=16.35 EndY=50 EndZ=0
  constraints (9):
    c: Coincident(g1,g0)
    c: Vertical(g1)
    c: Coincident(g2,g1)
    c: Coincident(g2,g0)
    c: Horizontal(g2)
    c: DistanceX(g-1,g0) = 16.35
    c: DistanceY(g-1,g0) = 10
    c: DistanceY(g-1,g0) = 50
    c: DistanceX(g-1,g1) = 126.35
FEATURE [PartDesign::Pocket] Pocket014
  AllowMultiFace = false
  BaseFeature = -> Pocket013
  Length = 5
  Length2 = 100
  Midplane = true
  Profile = -> Sketch040
  Type = 1
FEATURE [PartDesign::Fillet] Fillet002
  Base = -> Pocket014 [Edge17,Edge11]
  BaseFeature = -> Pocket014
  Radius = 9.525
  SupportTransform = true
  expr: Radius = 3 / 8 * 25.4
FEATURE [Sketcher::SketchObject] Sketch041
  MapMode = 5
  Placement = pos=(0,0,0) rot=(-0.57735,0.57735,0.57735;4.18879rad)
  Support = -> [YZ_Plane046]
  expr: Constraints[12] = 3 / 8 * 25.4
  sketch-geometry (8):
    g0: LineSegment StartX=-15.2375 StartY=15 StartZ=0 EndX=5.2375 EndY=15 EndZ=0
    g1: LineSegment StartX=10 StartY=10.2375 StartZ=0 EndX=10 EndY=-10.2375 EndZ=0
    g2: LineSegment StartX=5.2375 StartY=-15 StartZ=0 EndX=-15.2375 EndY=-15 EndZ=0
    g3: LineSegment StartX=-20 StartY=-10.2375 StartZ=0 EndX=-20 EndY=10.2375 EndZ=0
    g4: ArcOfCircle CenterX=5.2375 CenterY=10.2375 CenterZ=0 NormalX=0 NormalY=0 NormalZ=1 AngleXU=0 Radius=4.7625 StartAngle=0 EndAngle=1.5708
    g5: ArcOfCircle CenterX=-15.2375 CenterY=10.2375 CenterZ=0 NormalX=0 NormalY=0 NormalZ=1 AngleXU=0 Radius=4.7625 StartAngle=1.5708 EndAngle=3.14159
    g6: ArcOfCircle CenterX=-15.2375 CenterY=-10.2375 CenterZ=0 NormalX=0 NormalY=0 NormalZ=1 AngleXU=0 Radius=4.7625 StartAngle=3.14159 EndAngle=4.71239
    g7: ArcOfCircle CenterX=5.2375 CenterY=-10.2375 CenterZ=0 NormalX=0 NormalY=0 NormalZ=1 AngleXU=0 Radius=4.7625 StartAngle=4.71239 EndAngle=6.28319
  constraints (19):
    c: Horizontal(g0)
    c: Horizontal(g2)
    c: Vertical(g1)
    c: Vertical(g3)
    c: Tangent(g0,g4) = 1.5708
    c: Tangent(g1,g4) = 1.5708
    c: Tangent(g0,g5) = 1.5708
    c: Tangent(g3,g5) = 1.5708
    c: Tangent(g3,g6) = 1.5708
    c: Tangent(g2,g6) = 1.5708
    c: Tangent(g1,g7) = 1.5708
    c: Tangent(g2,g7) = 1.5708
    c: Diameter(g4) = 9.525
    c: Equal(g6,g7)
    c: DistanceY(g-1,g0) = 15
    c: DistanceX(g-1,g1) = 10
    c: Symmetric(g0,g2,g-1)
    c: Equal(g4,g7)
    c: DistanceX(g3,g-1) = 20
FEATURE [PartDesign::Pocket] Pocket015
  AllowMultiFace = false
  BaseFeature = -> Fillet002
  Length = 19
  Length2 = 100
  Profile = -> Sketch041
  Type = 0
FEATURE [Sketcher::SketchObject] Sketch042
  AttachmentOffset = pos=(0,0,6.35) rot=(0,0,1;0rad)
  MapMode = 5
  Placement = pos=(6.35,-1.4e-15,1.4e-15) rot=(0.57735,0.57735,0.57735;2.0944rad)
  Support = -> [YZ_Plane046]
  sketch-geometry (2):
    g0: Circle CenterX=-40 CenterY=49.85 CenterZ=0 NormalX=0 NormalY=0 NormalZ=1 AngleXU=0 Radius=2.505
    g1: Circle CenterX=40 CenterY=49.85 CenterZ=0 NormalX=0 NormalY=0 NormalZ=1 AngleXU=0 Radius=2.505
  constraints (5):
    c: DistanceX(g0,g-1) = 40
    c: Equal(g0,g1)
    c: Diameter(g1) = 5.01
    c: DistanceY(g-1,g1) = 49.85
    c: Symmetric(g1,g0,g-2)
FEATURE [PartDesign::Hole] Hole004
  AllowMultiFace = false
  BaseFeature = -> Pocket015
  Depth = 25
  DepthType = 1
  Diameter = 5.02
  DrillPoint = 1
  DrillPointAngle = 118
  HoleCutCountersinkAngle = 90
  HoleCutDepth = 2.18
  HoleCutDiameter = 10.1
  HoleCutType = 1
  ModelActualThread = false
  Profile = -> Sketch042
  Tapered = false
  TaperedAngle = 90
  ThreadAngle = 0
  ThreadClass = 0
  ThreadCutOffInner = 0
  ThreadCutOffOuter = 0
  ThreadDirection = 0
  ThreadFit = 0
  ThreadPitch = 0
  ThreadSize = 0
  ThreadType = 0
  Threaded = false
FEATURE [Sketcher::SketchObject] Sketch043
  AttachmentOffset = pos=(0,0,6.35) rot=(0,0,1;0rad)
  MapMode = 5
  Placement = pos=(6.35,-1.4e-15,1.4e-15) rot=(0.57735,0.57735,0.57735;2.0944rad)
  Support = -> [YZ_Plane046]
  sketch-geometry (2):
    g0: Circle CenterX=-40 CenterY=-49.85 CenterZ=0 NormalX=0 NormalY=0 NormalZ=1 AngleXU=0 Radius=3.57
    g1: Circle CenterX=40 CenterY=-49.85 CenterZ=0 NormalX=0 NormalY=0 NormalZ=1 AngleXU=0 Radius=3.57
  constraints (5):
    c: DistanceX(g0,g-1) = 40
    c: Equal(g0,g1)
    c: Diameter(g1) = 7.14
    c: Symmetric(g1,g0,g-2)
    c: DistanceY(g0,g-1) = 49.85
FEATURE [PartDesign::Hole] Hole005
  AllowMultiFace = false
  BaseFeature = -> Hole004
  Depth = 25
  DepthType = 1
  Diameter = 7.14
  DrillPoint = 1
  DrillPointAngle = 118
  HoleCutCountersinkAngle = 90
  HoleCutDepth = 2.18
  HoleCutDiameter = 12
  HoleCutType = 1
  ModelActualThread = false
  Profile = -> Sketch043
  Tapered = false
  TaperedAngle = 90
  ThreadAngle = 0
  ThreadClass = 0
  ThreadCutOffInner = 0
  ThreadCutOffOuter = 0
  ThreadDirection = 0
  ThreadFit = 0
  ThreadPitch = 0
  ThreadSize = 0
  ThreadType = 0
  Threaded = false
FEATURE [TechDraw::DrawSVGTemplate] Template008
  EditableTexts = Author=Alex Neufeld; DWG_num=2020-111; Date=25/05/2020; Revision=1; Scale=1:2; Subtitle=Machined from billet; Title=Carriage Block
  Height = 215.9
  Orientation = 1
  Width = 279.4
FEATURE [Sketcher::SketchObject] Sketch082
  AttachmentOffset = pos=(0,0,6.35) rot=(0,0,1;0rad)
  MapMode = 5
  Placement = pos=(6.35,-1.4e-15,1.4e-15) rot=(0.57735,0.57735,0.57735;2.0944rad)
  Support = -> [YZ_Plane046]
  sketch-geometry (7):
    g0: Circle CenterX=-38 CenterY=40 CenterZ=0 NormalX=0 NormalY=0 NormalZ=1 AngleXU=0 Radius=1.5
    g1: Circle CenterX=-38 CenterY=24 CenterZ=0 NormalX=0 NormalY=0 NormalZ=1 AngleXU=0 Radius=1.5
    g2: Circle CenterX=-8 CenterY=40 CenterZ=0 NormalX=0 NormalY=0 NormalZ=1 AngleXU=0 Radius=1.5
    g3: Circle CenterX=-8 CenterY=24 CenterZ=0 NormalX=0 NormalY=0 NormalZ=1 AngleXU=0 Radius=1.5
    g4: Circle CenterX=35 CenterY=0 CenterZ=0 NormalX=0 NormalY=0 NormalZ=1 AngleXU=0 Radius=1.5
    g5: Circle CenterX=25 CenterY=52 CenterZ=0 NormalX=0 NormalY=0 NormalZ=1 AngleXU=0 Radius=2.5
    g6: Circle CenterX=-35 CenterY=0 CenterZ=0 NormalX=0 NormalY=0 NormalZ=1 AngleXU=0 Radius=1.5
  constraints (21):
    c: Vertical(g2,g3)
    c: Vertical(g0,g1)
    c: Horizontal(g0,g2)
    c: Horizontal(g1,g3)
    c: Equal(g0,g1)
    c: Equal(g1,g3)
    c: Equal(g3,g2)
    c: Diameter(g2) = 3
    c: DistanceX(g3,g-1) = 8
    c: DistanceY(g-1,g3) = 24
    c: DistanceY(g3,g2) = 16
    c: DistanceX(g1,g3) = 30
    c: PointOnObject(g4,g-1)
    c: Diameter(g4) = 3
    c: DistanceX(g-1,g4) = 35
    c: Diameter(g5) = 5
    c: DistanceY(g-1,g5) = 52
    c: DistanceX(g-1,g5) = 25
    c: PointOnObject(g6,g-1)
    c: Equal(g6,g4)
    c: DistanceX(g6,g-1) = 35
FEATURE [PartDesign::Pocket] Pocket022
  BaseFeature = -> Hole005
  Length = 5
  Length2 = 100
  Profile = -> Sketch082
  Type = 1
FEATURE [Sketcher::SketchObject] Sketch083
  MapMode = 5
  Placement = pos=(0,0,0) rot=(1,0,0;1.5708rad)
  Support = -> [XZ_Plane046]
  sketch-geometry (3):
    g0: Circle CenterX=70 CenterY=0 CenterZ=0 NormalX=0 NormalY=0 NormalZ=1 AngleXU=0 Radius=2.55
    g1: Circle CenterX=120 CenterY=0 CenterZ=0 NormalX=0 NormalY=0 NormalZ=1 AngleXU=0 Radius=2.55
    g2: Circle CenterX=95 CenterY=0 CenterZ=0 NormalX=0 NormalY=0 NormalZ=1 AngleXU=0 Radius=2.55
  constraints (9):
    c: PointOnObject(g0,g-1)
    c: PointOnObject(g1,g-1)
    c: PointOnObject(g2,g-1)
    c: Equal(g0,g2)
    c: Equal(g2,g1)
    c: Diameter(g1) = 5.1
    c: DistanceX(g2,g1) = 25
    c: DistanceX(g0,g2) = 25
    c: DistanceX(g-1,g0) = 70
FEATURE [PartDesign::Pocket] Pocket023
  BaseFeature = -> Pocket022
  Length = 5
  Length2 = 100
  Profile = -> Sketch083
  Type = 1
FEATURE [PartDesign::Fillet] Fillet007
  Base = -> Pocket023 [Edge82,Edge17,Edge24,Edge13]
  BaseFeature = -> Pocket023
  Radius = 6.35
  SupportTransform = true
FEATURE [Sketcher::SketchObject] Sketch084
  MapMode = 5
  Support = -> [XY_Plane046]
  sketch-geometry (4):
    g0: LineSegment StartX=10 StartY=4 StartZ=0 EndX=54 EndY=4 EndZ=0
    g1: LineSegment StartX=54 StartY=4 StartZ=0 EndX=54 EndY=-21 EndZ=0
    g2: LineSegment StartX=54 StartY=-21 StartZ=0 EndX=10 EndY=-21 EndZ=0
    g3: LineSegment StartX=10 StartY=-21 StartZ=0 EndX=10 EndY=4 EndZ=0
  constraints (12):
    c: Coincident(g0,g1)
    c: Coincident(g1,g2)
    c: Coincident(g2,g3)
    c: Coincident(g3,g0)
    c: Horizontal(g0)
    c: Horizontal(g2)
    c: Vertical(g1)
    c: Vertical(g3)
    c: DistanceX(g-1,g0) = 10
    c: DistanceX(g2,g2) = 44
    c: DistanceY(g3,g3) = 25
    c: DistanceY(g-1,g0) = 4
FEATURE [PartDesign::Pocket] Pocket024
  BaseFeature = -> Fillet007
  Length = 20
  Length2 = 100
  Midplane = true
  Profile = -> Sketch084
  Type = 0
FEATURE [PartDesign::Body] Body016  label="Body"
  Group = -> [Sketch037,Pad016,Sketch038,Pad017,Sketch039,Pocket013,Sketch040,Pocket014,Fillet002,Sketch041,Pocket015,Sketch042,Hole004,Sketch043,Hole005,Sketch082,Pocket022,Sketch083,Pocket023,Fillet007,Sketch084,Pocket024]
  Origin = -> Origin046
  Tip = -> Pocket024
FEATURE [TechDraw::DrawViewAnnotation] Annotation009
  Font = Sans Serif
  LineSpace = 80
  LockPosition = false
  MaxWidth = -1
  Rotation = 0
  ScaleType = 0
  Text = Counterbore depth 2.18mm
  TextSize = 2.5
  TextStyle = 0
  X = 41.3094
  Y = 48.5238
FEATURE [PartDesign::CoordinateSystem] LCS_1
  AttacherType = Attacher::AttachEngine3D
  MapMode = 11
  Placement = pos=(70,8,1.8e-15) rot=(0.57735,-0.57735,0.57735;2.0944rad)
  Support = -> [Fillet007]
FEATURE [PartDesign::CoordinateSystem] LCS_2
  AttacherType = Attacher::AttachEngine3D
  MapMode = 11
  Placement = pos=(95,8,1.8e-15) rot=(0.57735,-0.57735,0.57735;2.0944rad)
  Support = -> [Fillet007]
FEATURE [PartDesign::CoordinateSystem] LCS_3
  AttacherType = Attacher::AttachEngine3D
  MapMode = 11
  Placement = pos=(120,8,1.8e-15) rot=(0.57735,-0.57735,0.57735;2.0944rad)
  Support = -> [Fillet007]
FEATURE [PartDesign::CoordinateSystem] LCS_4
  AttacherType = Attacher::AttachEngine3D
  AttachmentOffset = pos=(0,-15,0) rot=(0,0,1;0rad)
  MapMode = 45
  Placement = pos=(57.675,-1.1e-14,1.91e-14) rot=(0.57735,0.57735,0.57735;4.18879rad)
  Support = -> [Fillet007]
FEATURE [PartDesign::CoordinateSystem] LCS_5
  AttacherType = Attacher::AttachEngine3D
  MapMode = 11
  Placement = pos=(6.35,-38,40) rot=(0.707107,0,0.707107;3.14159rad)
  Support = -> [Fillet007]
FEATURE [PartDesign::CoordinateSystem] LCS_6
  AttacherType = Attacher::AttachEngine3D
  MapMode = 11
  Placement = pos=(6.35,-8,40) rot=(0.707107,0,0.707107;3.14159rad)
  Support = -> [Fillet007]
FEATURE [PartDesign::CoordinateSystem] LCS_7
  AttacherType = Attacher::AttachEngine3D
  MapMode = 11
  Placement = pos=(6.35,-38,24) rot=(0.707107,0,0.707107;3.14159rad)
  Support = -> [Fillet007]
FEATURE [PartDesign::CoordinateSystem] LCS_8
  AttacherType = Attacher::AttachEngine3D
  MapMode = 11
  Placement = pos=(6.35,-8,24) rot=(0.707107,0,0.707107;3.14159rad)
  Support = -> [Fillet007]
FEATURE [PartDesign::CoordinateSystem] LCS_9
  AttacherType = Attacher::AttachEngine3D
  MapMode = 11
  Placement = pos=(4.17,-40,49.85) rot=(0.57735,0.57735,0.57735;2.0944rad)
  Support = -> [Fillet007]
FEATURE [PartDesign::CoordinateSystem] LCS_10
  AttacherType = Attacher::AttachEngine3D
  MapMode = 11
  Placement = pos=(4.17,40,49.85) rot=(0.57735,0.57735,0.57735;2.0944rad)
  Support = -> [Fillet007]
FEATURE [PartDesign::CoordinateSystem] LCS_11
  AttacherType = Attacher::AttachEngine3D
  MapMode = 11
  Placement = pos=(0,-40,49.85) rot=(-0.57735,0.57735,0.57735;4.18879rad)
  Support = -> [Fillet007]
FEATURE [PartDesign::CoordinateSystem] LCS_12
  AttacherType = Attacher::AttachEngine3D
  MapMode = 11
  Placement = pos=(0,40,49.85) rot=(-0.57735,0.57735,0.57735;4.18879rad)
  Support = -> [Fillet007]
FEATURE [PartDesign::CoordinateSystem] LCS_13
  AttacherType = Attacher::AttachEngine3D
  MapMode = 11
  Placement = pos=(0,40,-49.85) rot=(-0.57735,0.57735,0.57735;4.18879rad)
  Support = -> [Fillet007]
FEATURE [PartDesign::CoordinateSystem] LCS_14
  AttacherType = Attacher::AttachEngine3D
  MapMode = 11
  Placement = pos=(0,-40,-49.85) rot=(-0.57735,0.57735,0.57735;4.18879rad)
  Support = -> [Fillet007]
FEATURE [PartDesign::CoordinateSystem] LCS_15
  AttacherType = Attacher::AttachEngine3D
  AttachmentOffset = pos=(6,0,0) rot=(0,0,1;0rad)
  MapMode = 45
  Placement = pos=(6.35,-23,38) rot=(0.707107,0,0.707107;3.14159rad)
  Support = -> [Fillet007]
FEATURE [App::Part] Part026  label="y_axis_carriage_block"
  Group = -> [Body016,LCS_1,LCS_2,LCS_3,LCS_4,LCS_5,LCS_6,LCS_7,LCS_8,LCS_9,LCS_10,LCS_11,LCS_12,LCS_13,LCS_14,LCS_15]
  Origin = -> Origin040
FEATURE [TechDraw::DrawViewPart] View009
  CoarseView = false
  Direction = (0.577,-0.577,0.577)
  Focus = 100
  HardHidden = false
  IsoCount = 0
  IsoHidden = false
  IsoVisible = false
  LockPosition = false
  Perspective = false
  Rotation = 0
  Scale = 0.33
  ScaleType = 0
  SeamHidden = false
  SeamVisible = true
  SmoothHidden = false
  SmoothVisible = true
  Source = -> [Part026]
  X = 34.7513
  XDirection = (0.707,0.707,0)
  Y = 180.756
FEATURE [TechDraw::DrawProjGroupItem] ProjItem029  label="Front008"
  CoarseView = false
  Direction = (0,-1,0)
  Focus = 100
  HardHidden = false
  IsoCount = 0
  IsoHidden = false
  IsoVisible = false
  LockPosition = true
  Perspective = false
  Rotation = 0
  RotationVector = (1,0,0)
  Scale = 0.5
  ScaleType = 2
  SeamHidden = false
  SeamVisible = true
  SmoothHidden = false
  SmoothVisible = true
  Source = -> [Part026]
  Type = 0
  X = 0
  XDirection = (1,0,0)
  Y = 0
FEATURE [TechDraw::DrawProjGroupItem] ProjItem030  label="Bottom006"
  CoarseView = false
  Direction = (0,0,-1)
  Focus = 100
  HardHidden = false
  IsoCount = 0
  IsoHidden = false
  IsoVisible = false
  LockPosition = true
  Perspective = false
  Rotation = 0
  RotationVector = (1,0,0)
  ScaleType = 2
  SeamHidden = false
  SeamVisible = true
  SmoothHidden = false
  SmoothVisible = true
  Source = -> [Part026]
  Type = 5
  X = 0
  XDirection = (1,0,0)
  Y = 75
FEATURE [TechDraw::DrawProjGroupItem] ProjItem031  label="Right004"
  CoarseView = false
  Direction = (1,-1e-16,0)
  Focus = 100
  HardHidden = false
  IsoCount = 0
  IsoHidden = false
  IsoVisible = false
  LockPosition = true
  Perspective = false
  Rotation = 0
  RotationVector = (1,0,0)
  ScaleType = 2
  SeamHidden = false
  SeamVisible = true
  SmoothHidden = false
  SmoothVisible = true
  Source = -> [Part026]
  Type = 2
  X = -78.175
  XDirection = (1e-16,1,0)
  Y = 0
FEATURE [TechDraw::DrawProjGroup] ProjGroup008
  Anchor = -> ProjItem029
  AutoDistribute = true
  LockPosition = true
  ProjectionType = 0
  Rotation = 0
  Scale = 0.5
  ScaleType = 2
  Source = -> [Part026]
  Views = -> [ProjItem029,ProjItem030,ProjItem031]
  X = 151.564
  Y = 83.8481
  spacingX = 15
  spacingY = 15
FEATURE [TechDraw::DrawViewDimExtent] DimExtent005
  Arbitrary = false
  ArbitraryTolerances = false
  CosmeticTags = 0b52134a-8e6d-49b5-af52-e823de50e186 | 81887f05-93b7-4f57-9f60-22745010a6d3
  DirExtent = 0
  FormatSpec = %.2f
  FormatSpecOverTolerance = %+.2f
  FormatSpecUnderTolerance = %+.2f
  Inverted = false
  LockPosition = false
  MeasureType = 1
  OverTolerance = 0
  References2D = -> [ProjItem031]
  Rotation = 0
  ScaleType = 0
  Source = -> [ProjItem031]
  TheoreticalExact = false
  Type = 1
  UnderTolerance = 0
  X = 0.546024
  Y = -36.8813
FEATURE [TechDraw::DrawViewDimExtent] DimExtent006
  Arbitrary = false
  ArbitraryTolerances = false
  CosmeticTags = 3ffed1fc-5ad0-4ec7-b127-2a2c0d19fe92 | 0dd20677-cea0-4880-986b-66a6b66657e0
  DirExtent = 1
  FormatSpec = %.2f
  FormatSpecOverTolerance = %+.2f
  FormatSpecUnderTolerance = %+.2f
  Inverted = false
  LockPosition = false
  MeasureType = 1
  OverTolerance = 0
  References2D = -> [ProjItem031]
  Rotation = 0
  ScaleType = 0
  Source = -> [ProjItem031]
  TheoreticalExact = false
  Type = 2
  UnderTolerance = 0
  X = -38.9861
  Y = 1.54868
FEATURE [TechDraw::DrawViewDimExtent] DimExtent007
  Arbitrary = false
  ArbitraryTolerances = false
  CosmeticTags = cf14e2b6-0178-4381-bba3-44740000f48a | 09ec5796-2379-4229-aecd-7de02c0fdcc3
  DirExtent = 0
  FormatSpec = %.2f
  FormatSpecOverTolerance = %+.2f
  FormatSpecUnderTolerance = %+.2f
  Inverted = false
  LockPosition = false
  MeasureType = 1
  OverTolerance = 0
  References2D = -> [ProjItem029]
  Rotation = 0
  ScaleType = 0
  Source = -> [ProjItem029]
  TheoreticalExact = false
  Type = 1
  UnderTolerance = 0
  X = -2.12632
  Y = -52.8642
FEATURE [TechDraw::DrawViewDetail] Detail
  AnchorPoint = (0.6,0.3,0)
  BaseView = -> ProjItem031
  CoarseView = false
  Direction = (1,-1e-16,0)
  Focus = 100
  HardHidden = false
  IsoCount = 0
  IsoHidden = false
  IsoVisible = false
  LockPosition = false
  Perspective = false
  Radius = 15
  Reference = 1
  Rotation = 0
  ScaleType = 0
  SeamHidden = false
  SeamVisible = true
  SmoothHidden = false
  SmoothVisible = true
  Source = -> [Part026]
  X = 239.468
  XDirection = (1e-16,1,0)
  Y = 166.543
FEATURE [TechDraw::DrawViewDimension] Dimension122
  Arbitrary = false
  ArbitraryTolerances = false
  FormatSpec = %.2f
  FormatSpecOverTolerance = %+.2f
  FormatSpecUnderTolerance = %+.2f
  Inverted = false
  LockPosition = false
  MeasureType = 1
  OverTolerance = 0
  References2D = -> [ProjItem031]
  Rotation = 0
  ScaleType = 0
  TheoreticalExact = false
  Type = 1
  UnderTolerance = 0
  X = -35.1344
  Y = 43.6728
FEATURE [TechDraw::DrawViewDimension] Dimension123
  Arbitrary = false
  ArbitraryTolerances = false
  FormatSpec = %.2f
  FormatSpecOverTolerance = %+.2f
  FormatSpecUnderTolerance = %+.2f
  Inverted = false
  LockPosition = false
  MeasureType = 1
  OverTolerance = 0
  References2D = -> [ProjItem031]
  Rotation = 0
  ScaleType = 0
  TheoreticalExact = false
  Type = 1
  UnderTolerance = 0
  X = -1.81485
  Y = 52.077
FEATURE [TechDraw::DrawViewDimension] Dimension124
  Arbitrary = false
  ArbitraryTolerances = false
  FormatSpec = %.2f
  FormatSpecOverTolerance = %+.2f
  FormatSpecUnderTolerance = %+.2f
  Inverted = false
  LockPosition = false
  MeasureType = 1
  OverTolerance = 0
  References2D = -> [ProjItem031]
  Rotation = 0
  ScaleType = 0
  TheoreticalExact = false
  Type = 1
  UnderTolerance = 0
  X = -5.76535
  Y = 36.2849
FEATURE [TechDraw::DrawViewDimension] Dimension125
  Arbitrary = false
  ArbitraryTolerances = false
  FormatSpec = %.2f
  FormatSpecOverTolerance = %+.2f
  FormatSpecUnderTolerance = %+.2f
  Inverted = false
  LockPosition = false
  MeasureType = 1
  OverTolerance = 0
  References2D = -> [ProjItem031]
  Rotation = 0
  ScaleType = 0
  TheoreticalExact = false
  Type = 1
  UnderTolerance = 0
  X = -22
  Y = 17.732
FEATURE [TechDraw::DrawViewDimension] Dimension126
  Arbitrary = false
  ArbitraryTolerances = false
  FormatSpec = %.2f
  FormatSpecOverTolerance = %+.2f
  FormatSpecUnderTolerance = %+.2f
  Inverted = false
  LockPosition = false
  MeasureType = 1
  OverTolerance = 0
  References2D = -> [ProjItem031]
  Rotation = 0
  ScaleType = 0
  TheoreticalExact = false
  Type = 1
  UnderTolerance = 0
  X = -10.718
  Y = 24.2808
FEATURE [TechDraw::DrawViewDimension] Dimension127
  Arbitrary = false
  ArbitraryTolerances = false
  FormatSpec = %.2f
  FormatSpecOverTolerance = %+.2f
  FormatSpecUnderTolerance = %+.2f
  Inverted = false
  LockPosition = false
  MeasureType = 1
  OverTolerance = 0
  References2D = -> [ProjItem031]
  Rotation = 0
  ScaleType = 0
  TheoreticalExact = false
  Type = 1
  UnderTolerance = 0
  X = -11.5378
  Y = -9.88744
FEATURE [TechDraw::DrawViewDimension] Dimension128
  Arbitrary = false
  ArbitraryTolerances = false
  FormatSpec = %.2f
  FormatSpecOverTolerance = %+.2f
  FormatSpecUnderTolerance = %+.2f
  Inverted = false
  LockPosition = false
  MeasureType = 1
  OverTolerance = 0
  References2D = -> [ProjItem031]
  Rotation = 0
  ScaleType = 0
  TheoreticalExact = false
  Type = 1
  UnderTolerance = 0
  X = -12.013
  Y = 5.78028
FEATURE [TechDraw::DrawViewDimension] Dimension129
  Arbitrary = false
  ArbitraryTolerances = false
  FormatSpec = %.2f
  FormatSpecOverTolerance = %+.2f
  FormatSpecUnderTolerance = %+.2f
  Inverted = false
  LockPosition = false
  MeasureType = 1
  OverTolerance = 0
  References2D = -> [ProjItem031]
  Rotation = 0
  ScaleType = 0
  TheoreticalExact = false
  Type = 2
  UnderTolerance = 0
  X = -50.7316
  Y = 30.446
FEATURE [TechDraw::DrawViewDimension] Dimension130
  Arbitrary = false
  ArbitraryTolerances = false
  FormatSpec = %.2f
  FormatSpecOverTolerance = %+.2f
  FormatSpecUnderTolerance = %+.2f
  Inverted = false
  LockPosition = false
  MeasureType = 1
  OverTolerance = 0
  References2D = -> [ProjItem031]
  Rotation = 0
  ScaleType = 0
  TheoreticalExact = false
  Type = 2
  UnderTolerance = 0
  X = 12.4007
  Y = 42.2097
FEATURE [TechDraw::DrawViewDimension] Dimension131
  Arbitrary = false
  ArbitraryTolerances = false
  FormatSpec = %.2f
  FormatSpecOverTolerance = %+.2f
  FormatSpecUnderTolerance = %+.2f
  Inverted = false
  LockPosition = false
  MeasureType = 1
  OverTolerance = 0
  References2D = -> [ProjItem031]
  Rotation = 0
  ScaleType = 0
  TheoreticalExact = false
  Type = 2
  UnderTolerance = 0
  X = -47.4173
  Y = 1.82714
FEATURE [TechDraw::DrawViewDimension] Dimension132
  Arbitrary = false
  ArbitraryTolerances = false
  FormatSpec = %.2f
  FormatSpecOverTolerance = %+.2f
  FormatSpecUnderTolerance = %+.2f
  Inverted = false
  LockPosition = false
  MeasureType = 1
  OverTolerance = 0
  References2D = -> [ProjItem029]
  Rotation = 0
  ScaleType = 0
  TheoreticalExact = false
  Type = 1
  UnderTolerance = 0
  X = -17.705
  Y = 21.9071
FEATURE [TechDraw::DrawViewDimension] Dimension133
  Arbitrary = false
  ArbitraryTolerances = false
  FormatSpec = %.2f
  FormatSpecOverTolerance = %+.2f
  FormatSpecUnderTolerance = %+.2f
  Inverted = false
  LockPosition = false
  MeasureType = 1
  OverTolerance = 0
  References2D = -> [ProjItem029]
  Rotation = 0
  ScaleType = 0
  TheoreticalExact = false
  Type = 1
  UnderTolerance = 0
  X = -5.86702
  Y = 36.381
FEATURE [TechDraw::DrawViewDimension] Dimension134
  Arbitrary = false
  ArbitraryTolerances = false
  FormatSpec = %.2f
  FormatSpecOverTolerance = %+.2f
  FormatSpecUnderTolerance = %+.2f
  Inverted = false
  LockPosition = false
  MeasureType = 1
  OverTolerance = 0
  References2D = -> [ProjItem029]
  Rotation = 0
  ScaleType = 0
  TheoreticalExact = false
  Type = 1
  UnderTolerance = 0
  X = -13.2974
  Y = -12.9991
FEATURE [TechDraw::DrawViewDimension] Dimension135
  Arbitrary = false
  ArbitraryTolerances = false
  FormatSpec = %.2f
  FormatSpecOverTolerance = %+.2f
  FormatSpecUnderTolerance = %+.2f
  Inverted = false
  LockPosition = false
  MeasureType = 1
  OverTolerance = 0
  References2D = -> [ProjItem029]
  Rotation = 0
  ScaleType = 0
  TheoreticalExact = false
  Type = 1
  UnderTolerance = 0
  X = -17.2834
  Y = -20.9932
FEATURE [TechDraw::DrawViewDimension] Dimension137
  Arbitrary = false
  ArbitraryTolerances = false
  FormatSpec = %.2f
  FormatSpecOverTolerance = %+.2f
  FormatSpecUnderTolerance = %+.2f
  Inverted = false
  LockPosition = false
  MeasureType = 1
  OverTolerance = 0
  References2D = -> [ProjItem029]
  Rotation = 0
  ScaleType = 0
  TheoreticalExact = false
  Type = 2
  UnderTolerance = 0
  X = -6.65506
  Y = 19.3725
FEATURE [TechDraw::DrawViewDimension] Dimension138
  Arbitrary = false
  ArbitraryTolerances = false
  FormatSpec = %.2f
  FormatSpecOverTolerance = %+.2f
  FormatSpecUnderTolerance = %+.2f
  Inverted = false
  LockPosition = false
  MeasureType = 1
  OverTolerance = 0
  References2D = -> [ProjItem029]
  Rotation = 0
  ScaleType = 0
  TheoreticalExact = false
  Type = 2
  UnderTolerance = 0
  X = -41.3114
  Y = 6.58101
FEATURE [TechDraw::DrawViewDimension] Dimension139
  Arbitrary = false
  ArbitraryTolerances = false
  FormatSpec = %.2f
  FormatSpecOverTolerance = %+.2f
  FormatSpecUnderTolerance = %+.2f
  Inverted = false
  LockPosition = false
  MeasureType = 1
  OverTolerance = 0
  References2D = -> [ProjItem031]
  Rotation = 0
  ScaleType = 0
  TheoreticalExact = false
  Type = 2
  UnderTolerance = 0
  X = -32.0512
  Y = 1.80996
FEATURE [TechDraw::DrawViewDimension] Dimension140
  Arbitrary = false
  ArbitraryTolerances = false
  FormatSpec = %.2f
  FormatSpecOverTolerance = %+.2f
  FormatSpecUnderTolerance = %+.2f
  Inverted = false
  LockPosition = false
  MeasureType = 1
  OverTolerance = 0
  References2D = -> [Detail]
  Rotation = 0
  ScaleType = 0
  TheoreticalExact = false
  Type = 2
  UnderTolerance = 0
  X = -21.7884
  Y = -0.002626
FEATURE [TechDraw::DrawViewDimension] Dimension141
  Arbitrary = false
  ArbitraryTolerances = false
  FormatSpec = %.2f
  FormatSpecOverTolerance = %+.2f
  FormatSpecUnderTolerance = %+.2f
  Inverted = false
  LockPosition = false
  MeasureType = 1
  OverTolerance = 0
  References2D = -> [Detail]
  Rotation = 0
  ScaleType = 0
  TheoreticalExact = false
  Type = 1
  UnderTolerance = 0
  X = -21.7021
  Y = 21.1806
FEATURE [TechDraw::DrawViewDimension] Dimension142
  Arbitrary = false
  ArbitraryTolerances = false
  FormatSpec = %.2f
  FormatSpecOverTolerance = %+.2f
  FormatSpecUnderTolerance = %+.2f
  Inverted = false
  LockPosition = false
  MeasureType = 1
  OverTolerance = 0
  References2D = -> [Detail]
  Rotation = 0
  ScaleType = 0
  TheoreticalExact = false
  Type = 2
  UnderTolerance = 0
  X = 20.1901
  Y = 0.000218
FEATURE [TechDraw::DrawViewDimension] Dimension143
  Arbitrary = false
  ArbitraryTolerances = false
  FormatSpec = %.2f
  FormatSpecOverTolerance = %+.2f
  FormatSpecUnderTolerance = %+.2f
  Inverted = false
  LockPosition = false
  MeasureType = 1
  OverTolerance = 0
  References2D = -> [ProjItem029]
  Rotation = 0
  ScaleType = 0
  TheoreticalExact = false
  Type = 2
  UnderTolerance = 0
  X = 47.1537
  Y = 13.8966
FEATURE [TechDraw::DrawViewDimension] Dimension144
  Arbitrary = false
  ArbitraryTolerances = false
  FormatSpec = %.2f
  FormatSpecOverTolerance = %+.2f
  FormatSpecUnderTolerance = %+.2f
  Inverted = false
  LockPosition = false
  MeasureType = 1
  OverTolerance = 0
  References2D = -> [ProjItem029]
  Rotation = 0
  ScaleType = 0
  TheoreticalExact = false
  Type = 1
  UnderTolerance = 0
  X = -14.2172
  Y = -32.7571
FEATURE [TechDraw::DrawViewDimension] Dimension145
  Arbitrary = false
  ArbitraryTolerances = false
  FormatSpec = %.2f
  FormatSpecOverTolerance = %+.2f
  FormatSpecUnderTolerance = %+.2f
  Inverted = false
  LockPosition = false
  MeasureType = 1
  OverTolerance = 0
  References2D = -> [ProjItem029]
  Rotation = 0
  ScaleType = 0
  TheoreticalExact = false
  Type = 1
  UnderTolerance = 0
  X = -6.15148
  Y = -38.2043
FEATURE [TechDraw::DrawViewDimension] Dimension146
  Arbitrary = false
  ArbitraryTolerances = false
  FormatSpec = %.2f
  FormatSpecOverTolerance = %+.2f
  FormatSpecUnderTolerance = %+.2f
  Inverted = false
  LockPosition = false
  MeasureType = 1
  OverTolerance = 0
  References2D = -> [ProjItem029]
  Rotation = 0
  ScaleType = 0
  TheoreticalExact = false
  Type = 1
  UnderTolerance = 0
  X = 1.21389
  Y = -44.8965
FEATURE [TechDraw::DrawViewDimension] Dimension147
  Arbitrary = false
  ArbitraryTolerances = false
  FormatSpec = %.2f
  FormatSpecOverTolerance = %+.2f
  FormatSpecUnderTolerance = %+.2f
  Inverted = false
  LockPosition = false
  MeasureType = 1
  OverTolerance = 0
  References2D = -> [ProjItem030]
  Rotation = 0
  ScaleType = 0
  TheoreticalExact = false
  Type = 1
  UnderTolerance = 0
  X = -5.8931
  Y = -28.1572
FEATURE [TechDraw::DrawViewDimension] Dimension151
  Arbitrary = false
  ArbitraryTolerances = false
  FormatSpec = %.2f
  FormatSpecOverTolerance = %+.2f
  FormatSpecUnderTolerance = %+.2f
  Inverted = false
  LockPosition = false
  MeasureType = 1
  OverTolerance = 0
  References2D = -> [ProjItem031]
  Rotation = 0
  ScaleType = 0
  TheoreticalExact = false
  Type = 2
  UnderTolerance = 0
  X = 20.9262
  Y = 15.2759
FEATURE [TechDraw::DrawViewDimension] Dimension152
  Arbitrary = false
  ArbitraryTolerances = false
  FormatSpec = %.2f
  FormatSpecOverTolerance = %+.2f
  FormatSpecUnderTolerance = %+.2f
  Inverted = false
  LockPosition = false
  MeasureType = 1
  OverTolerance = 0
  References2D = -> [ProjItem031]
  Rotation = 0
  ScaleType = 0
  TheoreticalExact = false
  Type = 2
  UnderTolerance = 0
  X = 28.2581
  Y = 12.2954
FEATURE [TechDraw::DrawViewDimension] Dimension153
  Arbitrary = false
  ArbitraryTolerances = false
  FormatSpec = %.2f
  FormatSpecOverTolerance = %+.2f
  FormatSpecUnderTolerance = %+.2f
  Inverted = false
  LockPosition = false
  MeasureType = 1
  OverTolerance = 0
  References2D = -> [ProjItem030]
  Rotation = 0
  ScaleType = 0
  TheoreticalExact = false
  Type = 2
  UnderTolerance = 0
  X = 30.8298
  Y = 12.7841
FEATURE [TechDraw::DrawViewDimension] Dimension154
  Arbitrary = false
  ArbitraryTolerances = false
  FormatSpec = %.2f
  FormatSpecOverTolerance = %+.2f
  FormatSpecUnderTolerance = %+.2f
  Inverted = false
  LockPosition = false
  MeasureType = 1
  OverTolerance = 0
  References2D = -> [ProjItem030]
  Rotation = 0
  ScaleType = 0
  TheoreticalExact = false
  Type = 2
  UnderTolerance = 0
  X = 36.2533
  Y = 10.6476
FEATURE [TechDraw::DrawViewDimension] Dimension155
  Arbitrary = false
  ArbitraryTolerances = false
  FormatSpec = %.2f
  FormatSpecOverTolerance = %+.2f
  FormatSpecUnderTolerance = %+.2f
  Inverted = false
  LockPosition = false
  MeasureType = 1
  OverTolerance = 0
  References2D = -> [ProjItem030]
  Rotation = 0
  ScaleType = 0
  TheoreticalExact = false
  Type = 2
  UnderTolerance = 0
  X = 41.3679
  Y = 8.79513
FEATURE [TechDraw::DrawViewDimension] Dimension156
  Arbitrary = false
  ArbitraryTolerances = false
  FormatSpec = %.2f
  FormatSpecOverTolerance = %+.2f
  FormatSpecUnderTolerance = %+.2f
  Inverted = false
  LockPosition = false
  MeasureType = 1
  OverTolerance = 0
  References2D = -> [ProjItem030]
  Rotation = 0
  ScaleType = 0
  TheoreticalExact = false
  Type = 2
  UnderTolerance = 0
  X = 46.9087
  Y = 7.44269
FEATURE [TechDraw::DrawViewDimension] Dimension157
  Arbitrary = false
  ArbitraryTolerances = false
  FormatSpec = %.2f
  FormatSpecOverTolerance = %+.2f
  FormatSpecUnderTolerance = %+.2f
  Inverted = false
  LockPosition = false
  MeasureType = 1
  OverTolerance = 0
  References2D = -> [ProjItem031]
  Rotation = 0
  ScaleType = 0
  TheoreticalExact = false
  Type = 1
  UnderTolerance = 0
  X = -15
  Y = -15.9719
FEATURE [TechDraw::DrawViewDimension] Dimension158
  Arbitrary = false
  ArbitraryTolerances = false
  FormatSpec = %.2f
  FormatSpecOverTolerance = %+.2f
  FormatSpecUnderTolerance = %+.2f
  Inverted = false
  LockPosition = false
  MeasureType = 1
  OverTolerance = 0
  References2D = -> [ProjItem031]
  Rotation = 0
  ScaleType = 0
  TheoreticalExact = false
  Type = 1
  UnderTolerance = 0
  X = 13.5722
  Y = 12.1156
FEATURE [TechDraw::DrawViewDimension] Dimension159
  Arbitrary = false
  ArbitraryTolerances = false
  FormatSpec = %.2f
  FormatSpecOverTolerance = %+.2f
  FormatSpecUnderTolerance = %+.2f
  Inverted = false
  LockPosition = false
  MeasureType = 1
  OverTolerance = 0
  References2D = -> [ProjItem029]
  Rotation = 0
  ScaleType = 0
  TheoreticalExact = false
  Type = 2
  UnderTolerance = 0
  X = 37.5072
  Y = 15.9656
FEATURE [TechDraw::DrawViewDimension] Dimension160
  Arbitrary = false
  ArbitraryTolerances = false
  FormatSpec = %.2f
  FormatSpecOverTolerance = %+.2f
  FormatSpecUnderTolerance = %+.2f
  Inverted = false
  LockPosition = false
  MeasureType = 1
  OverTolerance = 0
  References2D = -> [ProjItem029]
  Rotation = 0
  ScaleType = 0
  TheoreticalExact = false
  Type = 2
  UnderTolerance = 0
  X = 56.4313
  Y = 11.1361
FEATURE [TechDraw::DrawViewDimension] Dimension161
  Arbitrary = false
  ArbitraryTolerances = false
  FormatSpec = R%.2f
  FormatSpecOverTolerance = %+.2f
  FormatSpecUnderTolerance = %+.2f
  Inverted = false
  LockPosition = false
  MeasureType = 1
  OverTolerance = 0
  References2D = -> [ProjItem031]
  Rotation = 0
  ScaleType = 0
  TheoreticalExact = false
  Type = 4
  UnderTolerance = 0
  X = 32.4588
  Y = -32.0479
FEATURE [TechDraw::DrawViewDimension] Dimension162
  Arbitrary = false
  ArbitraryTolerances = false
  FormatSpec = ⌀%.2f
  FormatSpecOverTolerance = %+.2f
  FormatSpecUnderTolerance = %+.2f
  Inverted = false
  LockPosition = false
  MeasureType = 1
  OverTolerance = 0
  References2D = -> [ProjItem031]
  Rotation = 0
  ScaleType = 0
  TheoreticalExact = false
  Type = 5
  UnderTolerance = 0
  X = 32.272
  Y = -21.9629
FEATURE [TechDraw::DrawViewDimension] Dimension163
  Arbitrary = false
  ArbitraryTolerances = false
  FormatSpec = ⌀%.2f
  FormatSpecOverTolerance = %+.2f
  FormatSpecUnderTolerance = %+.2f
  Inverted = false
  LockPosition = false
  MeasureType = 1
  OverTolerance = 0
  References2D = -> [ProjItem031]
  Rotation = 0
  ScaleType = 0
  TheoreticalExact = false
  Type = 5
  UnderTolerance = 0
  X = 29.8068
  Y = -11.8779
FEATURE [TechDraw::DrawViewDimension] Dimension164
  Arbitrary = false
  ArbitraryTolerances = false
  FormatSpec = ⌀%.2f
  FormatSpecOverTolerance = %+.2f
  FormatSpecUnderTolerance = %+.2f
  Inverted = false
  LockPosition = false
  MeasureType = 1
  OverTolerance = 0
  References2D = -> [ProjItem029]
  Rotation = 0
  ScaleType = 0
  TheoreticalExact = false
  Type = 5
  UnderTolerance = 0
  X = 41.0827
  Y = -11.6026
FEATURE [TechDraw::DrawViewDimension] Dimension165
  Arbitrary = false
  ArbitraryTolerances = false
  FormatSpec = M%.0fx0.8
  FormatSpecOverTolerance = %+.2f
  FormatSpecUnderTolerance = %+.2f
  Inverted = false
  LockPosition = false
  MeasureType = 1
  OverTolerance = 0
  References2D = -> [ProjItem031]
  Rotation = 0
  ScaleType = 0
  TheoreticalExact = false
  Type = 5
  UnderTolerance = 0
  X = 25.7777
  Y = 38.4619
FEATURE [TechDraw::DrawViewDimension] Dimension166
  Arbitrary = false
  ArbitraryTolerances = false
  FormatSpec = M%.0fx0.5
  FormatSpecOverTolerance = %+.2f
  FormatSpecUnderTolerance = %+.2f
  Inverted = false
  LockPosition = false
  MeasureType = 1
  OverTolerance = 0
  References2D = -> [ProjItem031]
  Rotation = 0
  ScaleType = 0
  TheoreticalExact = false
  Type = 5
  UnderTolerance = 0
  X = 14.7301
  Y = -11.8659
FEATURE [TechDraw::DrawLeaderLine] LeaderLine009
  AutoHorizontal = true
  EndSymbol = 7
  LeaderParent = -> ProjItem031
  LockPosition = true
  Rotation = 0
  Scalable = false
  ScaleType = 0
  StartSymbol = 0
  WayPoints = (3) [(0,0,0),(-378.275,62.2952,0),(-303.302,62.2952,0)]
  X = -40.0313
  Y = -56.1373
FEATURE [TechDraw::DrawPage] Page008  label="carriage_dwg"
  KeepUpdated = false
  NextBalloonIndex = 1
  ProjectionType = 0
  Template = -> Template008
  Views = -> [View009,ProjGroup008,DimExtent005,DimExtent006,DimExtent007,Detail,Dimension122,Dimension123,Dimension124,Dimension125,Dimension126,Dimension127,Dimension128,Dimension129,Dimension130,Dimension131,Dimension132,Dimension133,Dimension134,Dimension135,Dimension137,Dimension138,Dimension139,Dimension140,Dimension141,Dimension142,Dimension143,Dimension144,Dimension145,Dimension146,Dimension147,+18 more]
